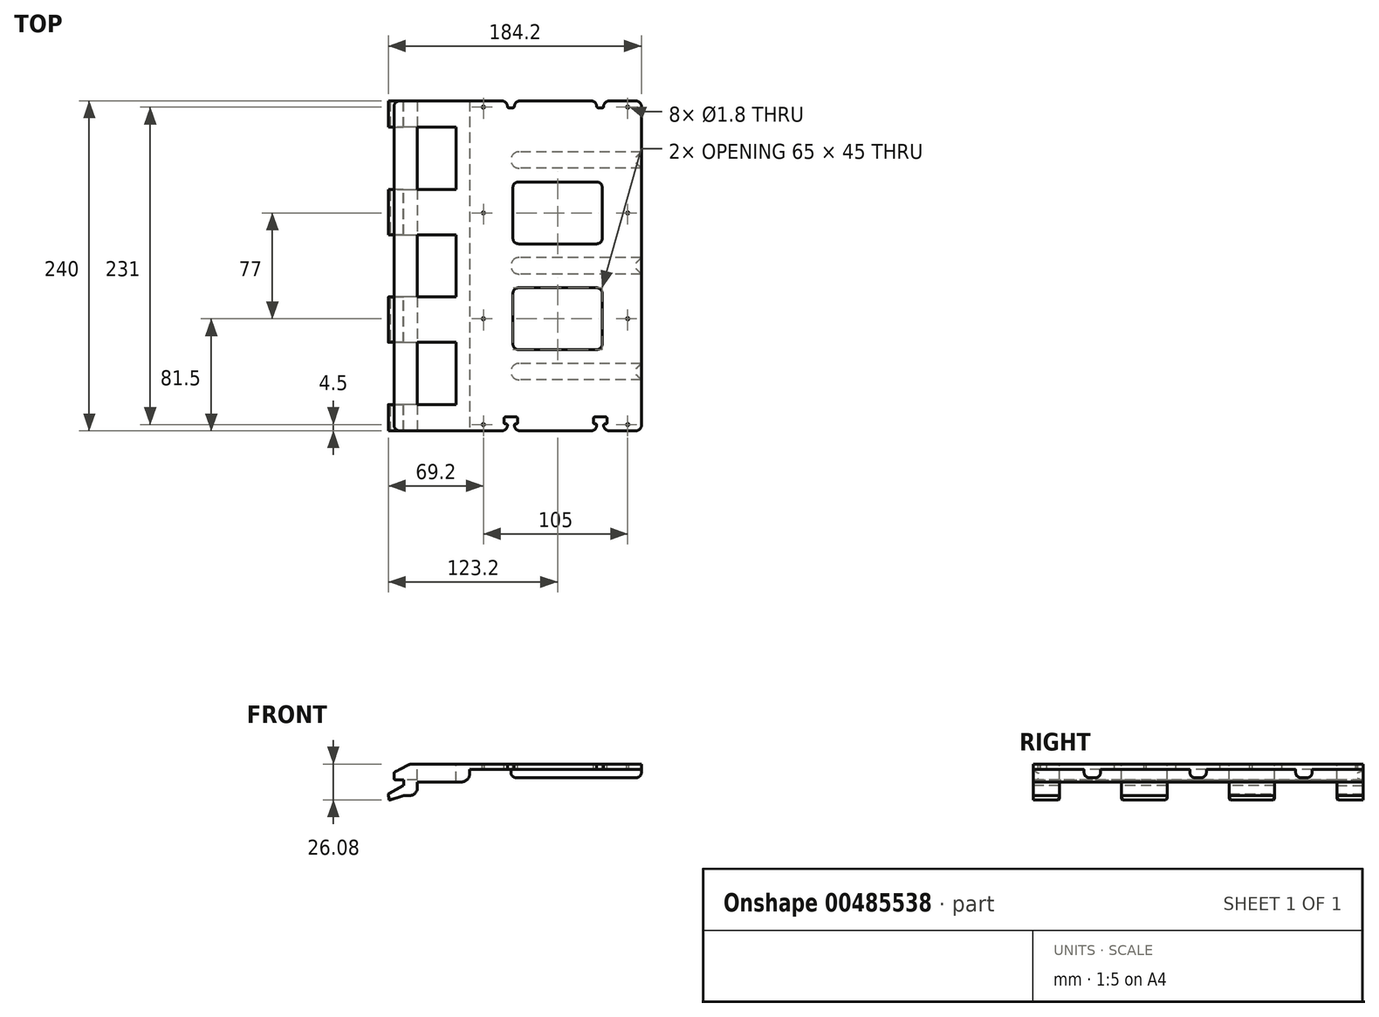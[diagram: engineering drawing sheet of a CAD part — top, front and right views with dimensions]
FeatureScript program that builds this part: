
annotation { "Feature Type Name" : "Feature", "Feature Type Description" : "" }
export const myFeature = defineFeature(function(context is Context, id is Id, definition is map)
    precondition{}
    {
        {
            var Q0;
            Q0=qCreatedBy(makeId("Top.planeOp"),FACE);
            var sketch = newSketch(context, id + "F0", { "sketchPlane" : qUnion([Q0])});
            skLineSegment(sketch, "E0", {"start": v(0, -197) * mm, "end": v(180, -197) * mm, "construction": true});
            skLineSegment(sketch, "E1", {"start": v(0, -43) * mm, "end": v(180, -43) * mm, "construction": true});
            skLineSegment(sketch, "E2", {"start": v(0, -158.5) * mm, "end": v(180, -158.5) * mm, "construction": true});
            skLineSegment(sketch, "E3", {"start": v(0, -81.5) * mm, "end": v(180, -81.5) * mm, "construction": true});
            skLineSegment(sketch, "E4", {"start": v(180, -203) * mm, "end": v(91, -203) * mm});
            skLineSegment(sketch, "E5", {"start": v(180, -191) * mm, "end": v(91, -191) * mm});
            skArc(sketch, "E6", {"start": v(91, -191) * mm, "mid": v(85, -197) * mm, "end": v(91, -203) * mm});
            skLineSegment(sketch, "E7", {"start": v(180, -126) * mm, "end": v(91, -126) * mm});
            skLineSegment(sketch, "E8", {"start": v(180, -114) * mm, "end": v(91, -114) * mm});
            skArc(sketch, "E9", {"start": v(91, -114) * mm, "mid": v(85, -120) * mm, "end": v(91, -126) * mm});
            skLineSegment(sketch, "E10", {"start": v(180, -49) * mm, "end": v(91, -49) * mm});
            skLineSegment(sketch, "E11", {"start": v(180, -37) * mm, "end": v(91, -37) * mm});
            skArc(sketch, "E12", {"start": v(91, -37) * mm, "mid": v(85, -43) * mm, "end": v(91, -49) * mm});
            skLineSegment(sketch, "E13", {"start": v(91, -240) * mm, "end": v(91, 0) * mm, "construction": true});
            skCircle(sketch, "E14", {"center": v(65, -158.5) * mm, "radius": 0.9 * mm});
            skCircle(sketch, "E15", {"center": v(65, -81.5) * mm, "radius": 0.9 * mm});
            skCircle(sketch, "E16", {"center": v(170, -158.5) * mm, "radius": 0.9 * mm});
            skCircle(sketch, "E17", {"center": v(170, -81.5) * mm, "radius": 0.9 * mm});
            skLineSegment(sketch, "E18.bottom", {"start": v(180, -240) * mm, "end": v(0, -240) * mm});
            skLineSegment(sketch, "E18.top", {"start": v(180, 0) * mm, "end": v(0, 0) * mm});
            skLineSegment(sketch, "E18.left", {"start": v(180, -240) * mm, "end": v(180, 0) * mm});
            skLineSegment(sketch, "E18.right", {"start": v(0, -240) * mm, "end": v(0, 0) * mm});
            skLineSegment(sketch, "E19", {"start": v(5, 0) * mm, "end": v(5, -240) * mm});
            skLineSegment(sketch, "E20", {"start": v(0, -120) * mm, "end": v(180, -120) * mm, "construction": true});
            skLineSegment(sketch, "E21", {"start": v(17, 0) * mm, "end": v(17, -240) * mm});
            skLineSegment(sketch, "E22", {"start": v(55, 0) * mm, "end": v(55, -240) * mm});
            skLineSegment(sketch, "E23", {"start": v(0, -97.4) * mm, "end": v(45, -97.4) * mm});
            skLineSegment(sketch, "E24", {"start": v(45, -97.4) * mm, "end": v(45, -142.6) * mm});
            skLineSegment(sketch, "E25", {"start": v(45, -142.6) * mm, "end": v(0, -142.6) * mm});
            skLineSegment(sketch, "E26", {"start": v(0, -175.7) * mm, "end": v(45, -175.7) * mm});
            skLineSegment(sketch, "E27", {"start": v(45, -175.7) * mm, "end": v(45, -220.9) * mm});
            skLineSegment(sketch, "E28", {"start": v(45, -220.9) * mm, "end": v(0, -220.9) * mm});
            skLineSegment(sketch, "E29", {"start": v(0, -64.3) * mm, "end": v(45, -64.3) * mm});
            skLineSegment(sketch, "E30", {"start": v(45, -64.3) * mm, "end": v(45, -19.1) * mm});
            skLineSegment(sketch, "E31", {"start": v(45, -19.1) * mm, "end": v(0, -19.1) * mm});
            skLineSegment(sketch, "E32", {"start": v(0, -235.5) * mm, "end": v(180, -235.5) * mm, "construction": true});
            skLineSegment(sketch, "E33", {"start": v(0, -4.5) * mm, "end": v(180, -4.5) * mm, "construction": true});
            skCircle(sketch, "E34", {"center": v(65, -235.5) * mm, "radius": 0.9 * mm});
            skCircle(sketch, "E35", {"center": v(65, -4.5) * mm, "radius": 0.9 * mm});
            skCircle(sketch, "E36", {"center": v(170, -4.5) * mm, "radius": 0.9 * mm});
            skCircle(sketch, "E37", {"center": v(170, -235.5) * mm, "radius": 0.9 * mm});
            skLineSegment(sketch, "E38.bottom", {"start": v(151.5, -104) * mm, "end": v(86.5, -104) * mm});
            skLineSegment(sketch, "E38.top", {"start": v(151.5, -59) * mm, "end": v(86.5, -59) * mm});
            skLineSegment(sketch, "E38.left", {"start": v(151.5, -104) * mm, "end": v(151.5, -59) * mm});
            skLineSegment(sketch, "E38.right", {"start": v(86.5, -104) * mm, "end": v(86.5, -59) * mm});
            skPoint(sketch, "E38.middle", {"position": v(119, -81.5) * mm});
            skLineSegment(sketch, "E39.bottom", {"start": v(151.5, -181) * mm, "end": v(86.5, -181) * mm});
            skLineSegment(sketch, "E39.top", {"start": v(151.5, -136) * mm, "end": v(86.5, -136) * mm});
            skLineSegment(sketch, "E39.left", {"start": v(151.5, -181) * mm, "end": v(151.5, -136) * mm});
            skLineSegment(sketch, "E39.right", {"start": v(86.5, -181) * mm, "end": v(86.5, -136) * mm});
            skPoint(sketch, "E39.middle", {"position": v(119, -158.5) * mm});
            skPoint(sketch, "E40.centerSnap0", {"position": v(119, -181) * mm});
            skLineSegment(sketch, "E41.bottom", {"start": v(82.5, -240) * mm, "end": v(87.5, -240) * mm});
            skLineSegment(sketch, "E41.top", {"start": v(82.5, -235) * mm, "end": v(87.5, -235) * mm});
            skLineSegment(sketch, "E41.left", {"start": v(82.5, -240) * mm, "end": v(82.5, -235) * mm});
            skLineSegment(sketch, "E41.right", {"start": v(87.5, -240) * mm, "end": v(87.5, -235) * mm});
            skLineSegment(sketch, "E42.bottom", {"start": v(80, -235) * mm, "end": v(90, -235) * mm});
            skLineSegment(sketch, "E42.top", {"start": v(80, -230) * mm, "end": v(90, -230) * mm});
            skLineSegment(sketch, "E42.left", {"start": v(80, -235) * mm, "end": v(80, -230) * mm});
            skLineSegment(sketch, "E42.right", {"start": v(90, -235) * mm, "end": v(90, -230) * mm});
            skLineSegment(sketch, "E43", {"start": v(85, -235) * mm, "end": v(85, -230) * mm, "construction": true});
            skLineSegment(sketch, "E44.bottom", {"start": v(147.5, -240) * mm, "end": v(152.5, -240) * mm});
            skLineSegment(sketch, "E44.top", {"start": v(147.5, -235) * mm, "end": v(152.5, -235) * mm});
            skLineSegment(sketch, "E44.left", {"start": v(147.5, -240) * mm, "end": v(147.5, -235) * mm});
            skLineSegment(sketch, "E44.right", {"start": v(152.5, -240) * mm, "end": v(152.5, -235) * mm});
            skLineSegment(sketch, "E45.bottom", {"start": v(145, -235) * mm, "end": v(155, -235) * mm});
            skLineSegment(sketch, "E45.top", {"start": v(145, -230) * mm, "end": v(155, -230) * mm});
            skLineSegment(sketch, "E45.left", {"start": v(145, -235) * mm, "end": v(145, -230) * mm});
            skLineSegment(sketch, "E45.right", {"start": v(155, -235) * mm, "end": v(155, -230) * mm});
            skLineSegment(sketch, "E46", {"start": v(150, -235) * mm, "end": v(150, -230) * mm, "construction": true});
            skLineSegment(sketch, "E47", {"start": v(150, -240) * mm, "end": v(150, -235) * mm, "construction": true});
            skLineSegment(sketch, "E48.bottom", {"start": v(152.5, 0) * mm, "end": v(147.5, 0) * mm});
            skLineSegment(sketch, "E48.top", {"start": v(152.5, -5) * mm, "end": v(147.5, -5) * mm});
            skLineSegment(sketch, "E48.left", {"start": v(152.5, 0) * mm, "end": v(152.5, -5) * mm});
            skLineSegment(sketch, "E48.right", {"start": v(147.5, 0) * mm, "end": v(147.5, -5) * mm});
            skLineSegment(sketch, "E49", {"start": v(150, 0) * mm, "end": v(150, -10) * mm, "construction": true});
            skPoint(sketch, "E49.endSnap0", {"position": v(150, -5) * mm});
            skLineSegment(sketch, "E50.bottom", {"start": v(145, -5) * mm, "end": v(155, -5) * mm});
            skLineSegment(sketch, "E50.top", {"start": v(145, -10) * mm, "end": v(155, -10) * mm});
            skLineSegment(sketch, "E50.left", {"start": v(145, -5) * mm, "end": v(145, -10) * mm});
            skLineSegment(sketch, "E50.right", {"start": v(155, -5) * mm, "end": v(155, -10) * mm});
            skLineSegment(sketch, "E51.bottom", {"start": v(82.5, 0) * mm, "end": v(87.5, 0) * mm});
            skLineSegment(sketch, "E51.top", {"start": v(82.5, -5) * mm, "end": v(87.5, -5) * mm});
            skLineSegment(sketch, "E51.left", {"start": v(82.5, 0) * mm, "end": v(82.5, -5) * mm});
            skLineSegment(sketch, "E51.right", {"start": v(87.5, 0) * mm, "end": v(87.5, -5) * mm});
            skLineSegment(sketch, "E52", {"start": v(85, 0) * mm, "end": v(85, -10) * mm, "construction": true});
            skLineSegment(sketch, "E53.bottom", {"start": v(90, -5) * mm, "end": v(80, -5) * mm});
            skLineSegment(sketch, "E53.top", {"start": v(90, -10) * mm, "end": v(80, -10) * mm});
            skLineSegment(sketch, "E53.left", {"start": v(90, -5) * mm, "end": v(90, -10) * mm});
            skLineSegment(sketch, "E53.right", {"start": v(80, -5) * mm, "end": v(80, -10) * mm});
            skSolve(sketch);
        }
        {
            var Q0;
            {var subQ7=sQuery(id+"F0.wireOp",EDGE,"E4");Q0=makeQuery(id+"F0.imprint","IMPRINT",FACE,{"disambiguationData":[TD([[makeQuery(id+"F0.imprint","IMPRINT",EDGE,{"derivedFrom":subQ7}),1.0]])]});}
            var Q1;
            {var subQ0=sQuery(id+"F0.wireOp",EDGE,"E4");Q1=makeQuery(id+"F0.imprint","IMPRINT",FACE,{"disambiguationData":[TD([[makeQuery(id+"F0.imprint","IMPRINT",EDGE,{"derivedFrom":subQ0}),-1.0]])]});}
            var Q2;
            {var subQ0=sQuery(id+"F0.wireOp",EDGE,"E7");Q2=makeQuery(id+"F0.imprint","IMPRINT",FACE,{"disambiguationData":[TD([[makeQuery(id+"F0.imprint","IMPRINT",EDGE,{"derivedFrom":subQ0}),-1.0]])]});}
            var Q3;
            {var subQ0=sQuery(id+"F0.wireOp",EDGE,"E10");Q3=makeQuery(id+"F0.imprint","IMPRINT",FACE,{"disambiguationData":[TD([[makeQuery(id+"F0.imprint","IMPRINT",EDGE,{"derivedFrom":subQ0}),-1.0]])]});}
            var Q4;
            Q4=makeQuery(id+"F0.imprint","IMPRINT",FACE,{"disambiguationData":[TD([[makeQuery(id+"F0.imprint","IMPRINT",EDGE,{"derivedFrom":sQuery(id+"F0.wireOp",EDGE,"E53.top")}),-1.0]])]});
            var Q5;
            Q5=makeQuery(id+"F0.imprint","IMPRINT",FACE,{"disambiguationData":[TD([[makeQuery(id+"F0.imprint","IMPRINT",EDGE,{"derivedFrom":sQuery(id+"F0.wireOp",EDGE,"E51.bottom")}),-1.0]])]});
            var Q6;
            Q6=makeQuery(id+"F0.imprint","IMPRINT",FACE,{"disambiguationData":[TD([[makeQuery(id+"F0.imprint","IMPRINT",EDGE,{"derivedFrom":sQuery(id+"F0.wireOp",EDGE,"E48.bottom")}),1.0]])]});
            var Q7;
            Q7=makeQuery(id+"F0.imprint","IMPRINT",FACE,{"disambiguationData":[TD([[makeQuery(id+"F0.imprint","IMPRINT",EDGE,{"derivedFrom":sQuery(id+"F0.wireOp",EDGE,"E50.top")}),1.0]])]});
            extrude(context, id + "F1", {"entities" : qUnion([Q0, Q1, Q2, Q3, Q4, Q5, Q6, Q7]), "oppositeDirection" : true, "depth" : 4 * mm});
        }
        {
            var Q0;
            {var subQ0=sQuery(id+"F0.wireOp",EDGE,"E21");Q0=makeQuery(id+"F0.imprint","IMPRINT",FACE,{"disambiguationData":[TD([[makeQuery(id+"F0.imprint","IMPRINT",EDGE,{"derivedFrom":subQ0}),1.0]])]});}
            var Q1;
            {var subQ5=sQuery(id+"F0.wireOp",EDGE,"n4lQ4PQO-9XsQ-tz0W-XekK-HpTfJCge4sbG");Q1=makeQuery(id+"F0.imprint","IMPRINT",FACE,{"disambiguationData":[TD([[makeQuery(id+"F0.imprint","IMPRINT",EDGE,{"derivedFrom":subQ5}),1.0]])]});}
            var Q2;
            {var subQ5=sQuery(id+"F0.wireOp",EDGE,"NRY2d1nv-D3un-2PJu-Z2eF-jLOu5DY2E8th");Q2=makeQuery(id+"F0.imprint","IMPRINT",FACE,{"disambiguationData":[TD([[makeQuery(id+"F0.imprint","IMPRINT",EDGE,{"derivedFrom":subQ5}),1.0]])]});}
            extrude(context, id + "F2", {"entities" : qUnion([Q0, Q1, Q2]), "operationType" : NewBodyOperationType.ADD, "oppositeDirection" : true, "depth" : 13 * mm});
        }
        {
            var Q0;
            {var subQ0=sQuery(id+"F0.wireOp",EDGE,"E19");var subQ1=sQuery(id+"F0.wireOp",EDGE,"E18.bottom");var subQ2=makeQuery(id+"F0.imprint","INTERSECT",VERTEX,{"derivedFrom":[subQ1,subQ0]});Q0=makeQuery(id+"F0.imprint","IMPRINT",FACE,{"disambiguationData":[TD([[makeQuery(id+"F0.imprint","IMPRINT",EDGE,{"disambiguationData":[TD([[subQ2,1.0]])],"derivedFrom":subQ1}),-1.0]])]});}
            var Q1;
            {var subQ0=sQuery(id+"F0.wireOp",EDGE,"E19");var subQ1=sQuery(id+"F0.wireOp",EDGE,"E18.top");var subQ2=makeQuery(id+"F0.imprint","INTERSECT",VERTEX,{"derivedFrom":[subQ1,subQ0]});Q1=makeQuery(id+"F0.imprint","IMPRINT",FACE,{"disambiguationData":[TD([[makeQuery(id+"F0.imprint","IMPRINT",EDGE,{"disambiguationData":[TD([[subQ2,1.0]])],"derivedFrom":subQ1}),1.0]])]});}
            var Q2;
            {var subQ0=sQuery(id+"F0.wireOp",EDGE,"E29");var subQ1=sQuery(id+"F0.wireOp",EDGE,"E19");var subQ2=makeQuery(id+"F0.imprint","INTERSECT",VERTEX,{"derivedFrom":[subQ1,subQ0]});Q2=makeQuery(id+"F0.imprint","IMPRINT",FACE,{"disambiguationData":[TD([[makeQuery(id+"F0.imprint","IMPRINT",EDGE,{"disambiguationData":[TD([[subQ2,-1.0]])],"derivedFrom":subQ1}),1.0]])]});}
            var Q3;
            {var subQ0=sQuery(id+"F0.wireOp",EDGE,"E25");var subQ1=sQuery(id+"F0.wireOp",EDGE,"E19");var subQ2=makeQuery(id+"F0.imprint","INTERSECT",VERTEX,{"derivedFrom":[subQ1,subQ0]});Q3=makeQuery(id+"F0.imprint","IMPRINT",FACE,{"disambiguationData":[TD([[makeQuery(id+"F0.imprint","IMPRINT",EDGE,{"disambiguationData":[TD([[subQ2,-1.0]])],"derivedFrom":subQ1}),1.0]])]});}
            extrude(context, id + "F3", {"entities" : qUnion([Q0, Q1, Q2, Q3]), "operationType" : NewBodyOperationType.ADD, "oppositeDirection" : true, "depth" : 23 * mm});
        }
        {
            var Q0;
            {var subQ0=sQuery(id+"F0.wireOp",EDGE,"E18.right");var subQ1=sQuery(id+"F0.wireOp",EDGE,"E18.bottom");var subQ2=makeQuery(id+"F0.imprint","INTERSECT",VERTEX,{"derivedFrom":[subQ1,subQ0]});Q0=makeQuery(id+"F0.imprint","IMPRINT",FACE,{"disambiguationData":[TD([[makeQuery(id+"F0.imprint","IMPRINT",EDGE,{"disambiguationData":[TD([[subQ2,1.0]])],"derivedFrom":subQ1}),-1.0]])]});}
            var Q1;
            {var subQ0=sQuery(id+"F0.wireOp",EDGE,"E18.right");var subQ1=sQuery(id+"F0.wireOp",EDGE,"E18.top");var subQ2=makeQuery(id+"F0.imprint","INTERSECT",VERTEX,{"derivedFrom":[subQ1,subQ0]});Q1=makeQuery(id+"F0.imprint","IMPRINT",FACE,{"disambiguationData":[TD([[makeQuery(id+"F0.imprint","IMPRINT",EDGE,{"disambiguationData":[TD([[subQ2,1.0]])],"derivedFrom":subQ1}),1.0]])]});}
            var Q2;
            {var subQ0=sQuery(id+"F0.wireOp",EDGE,"E25");var subQ1=sQuery(id+"F0.wireOp",EDGE,"E18.right");var subQ2=makeQuery(id+"F0.imprint","INTERSECT",VERTEX,{"derivedFrom":[subQ1,subQ0]});Q2=makeQuery(id+"F0.imprint","IMPRINT",FACE,{"disambiguationData":[TD([[makeQuery(id+"F0.imprint","IMPRINT",EDGE,{"disambiguationData":[TD([[subQ2,1.0]])],"derivedFrom":subQ1}),-1.0]])]});}
            var Q3;
            {var subQ0=sQuery(id+"F0.wireOp",EDGE,"E23");var subQ1=sQuery(id+"F0.wireOp",EDGE,"E18.right");var subQ2=makeQuery(id+"F0.imprint","INTERSECT",VERTEX,{"derivedFrom":[subQ1,subQ0]});Q3=makeQuery(id+"F0.imprint","IMPRINT",FACE,{"disambiguationData":[TD([[makeQuery(id+"F0.imprint","IMPRINT",EDGE,{"disambiguationData":[TD([[subQ2,-1.0]])],"derivedFrom":subQ1}),-1.0]])]});}
            var Q4;
            {var subQ0=sQuery(id+"F0.wireOp",EDGE,"E26");var subQ1=sQuery(id+"F0.wireOp",EDGE,"E18.right");var subQ2=makeQuery(id+"F0.imprint","INTERSECT",VERTEX,{"derivedFrom":[subQ1,subQ0]});Q4=makeQuery(id+"F0.imprint","IMPRINT",FACE,{"disambiguationData":[TD([[makeQuery(id+"F0.imprint","IMPRINT",EDGE,{"disambiguationData":[TD([[subQ2,1.0]])],"derivedFrom":subQ1}),-1.0]])]});}
            var Q5;
            {var subQ0=sQuery(id+"F0.wireOp",EDGE,"E23");var subQ1=sQuery(id+"F0.wireOp",EDGE,"E18.right");var subQ2=makeQuery(id+"F0.imprint","INTERSECT",VERTEX,{"derivedFrom":[subQ1,subQ0]});Q5=makeQuery(id+"F0.imprint","IMPRINT",FACE,{"disambiguationData":[TD([[makeQuery(id+"F0.imprint","IMPRINT",EDGE,{"disambiguationData":[TD([[subQ2,1.0]])],"derivedFrom":subQ1}),-1.0]])]});}
            var Q6;
            {var subQ0=sQuery(id+"F0.wireOp",EDGE,"E29");var subQ1=sQuery(id+"F0.wireOp",EDGE,"E18.right");var subQ2=makeQuery(id+"F0.imprint","INTERSECT",VERTEX,{"derivedFrom":[subQ1,subQ0]});Q6=makeQuery(id+"F0.imprint","IMPRINT",FACE,{"disambiguationData":[TD([[makeQuery(id+"F0.imprint","IMPRINT",EDGE,{"disambiguationData":[TD([[subQ2,-1.0]])],"derivedFrom":subQ1}),-1.0]])]});}
            var Q7;
            {var subQ0=sQuery(id+"F0.wireOp",EDGE,"E26");var subQ1=sQuery(id+"F0.wireOp",EDGE,"E19");var subQ2=makeQuery(id+"F0.imprint","INTERSECT",VERTEX,{"derivedFrom":[subQ1,subQ0]});Q7=makeQuery(id+"F0.imprint","IMPRINT",FACE,{"disambiguationData":[TD([[makeQuery(id+"F0.imprint","IMPRINT",EDGE,{"disambiguationData":[TD([[subQ2,-1.0]])],"derivedFrom":subQ1}),1.0]])]});}
            var Q8;
            {var subQ0=sQuery(id+"F0.wireOp",EDGE,"E23");var subQ1=sQuery(id+"F0.wireOp",EDGE,"E19");var subQ2=makeQuery(id+"F0.imprint","INTERSECT",VERTEX,{"derivedFrom":[subQ1,subQ0]});Q8=makeQuery(id+"F0.imprint","IMPRINT",FACE,{"disambiguationData":[TD([[makeQuery(id+"F0.imprint","IMPRINT",EDGE,{"disambiguationData":[TD([[subQ2,-1.0]])],"derivedFrom":subQ1}),1.0]])]});}
            var Q9;
            {var subQ0=sQuery(id+"F0.wireOp",EDGE,"E31");var subQ1=sQuery(id+"F0.wireOp",EDGE,"E19");var subQ2=makeQuery(id+"F0.imprint","INTERSECT",VERTEX,{"derivedFrom":[subQ1,subQ0]});Q9=makeQuery(id+"F0.imprint","IMPRINT",FACE,{"disambiguationData":[TD([[makeQuery(id+"F0.imprint","IMPRINT",EDGE,{"disambiguationData":[TD([[subQ2,-1.0]])],"derivedFrom":subQ1}),1.0]])]});}
            var Q10;
            Q10=makeQuery(id+"F2.opExtrude","CAP_FACE",FACE,{"disambiguationData":[OSD([sQuery(id+"F0.wireOp",EDGE,"E14"),sQuery(id+"F0.wireOp",EDGE,"E15"),sQuery(id+"F0.wireOp",EDGE,"E18.bottom"),sQuery(id+"F0.wireOp",EDGE,"E18.top"),sQuery(id+"F0.wireOp",EDGE,"E21"),sQuery(id+"F0.wireOp",EDGE,"E22")])],"isStart":false});
            extrude(context, id + "F4", {"entities" : qUnion([Q0, Q1, Q2, Q3, Q4, Q5, Q6, Q7, Q8, Q9]), "operationType" : NewBodyOperationType.ADD, "oppositeDirection" : true, "endBoundEntityFace" : qUnion([Q10]), "depth" : 11.5 * mm});
        }
        {
            var Q0;
            {var subQ0=sQuery(id+"F0.wireOp",EDGE,"E18.bottom");Q0=makeQuery(id+"F4.boolean.opBoolean","MERGE",FACE,{"derivedFrom":[makeQuery(id+"F3.boolean.opBoolean","MERGE",FACE,{"derivedFrom":[makeQuery(id+"F2.boolean.opBoolean","MERGE",FACE,{"derivedFrom":[makeQuery(id+"F1.opExtrude","SWEPT_FACE",FACE,{"disambiguationData":[OSD([subQ0])]}),makeQuery(id+"F2.opExtrude","SWEPT_FACE",FACE,{"disambiguationData":[OSD([subQ0])]})]}),makeQuery(id+"F3.opExtrude","SWEPT_FACE",FACE,{"disambiguationData":[OSD([subQ0])]})]}),makeQuery(id+"F4.opExtrude","SWEPT_FACE",FACE,{"disambiguationData":[OSD([subQ0])]})]});}
            var sketch = newSketch(context, id + "F5", { "sketchPlane" : qUnion([Q0])});
            skLineSegment(sketch, "E54.bottom", {"start": v(5, -11.5) * mm, "end": v(7, -11.5) * mm});
            skLineSegment(sketch, "E54.top", {"start": v(5, -15.5) * mm, "end": v(7, -15.5) * mm});
            skLineSegment(sketch, "E54.left", {"start": v(5, -11.5) * mm, "end": v(5, -15.5) * mm});
            skLineSegment(sketch, "E54.right", {"start": v(7, -11.5) * mm, "end": v(7, -15.5) * mm});
            skSolve(sketch);
        }
        {
            var Q0;
            Q0=makeQuery(id+"F5.imprint","IMPRINT",FACE,{"disambiguationData":[TD([[makeQuery(id+"F5.imprint","IMPRINT",EDGE,{"derivedFrom":sQuery(id+"F5.wireOp",EDGE,"E54.bottom")}),-1.0]])]});
            var Q1;
            {var subQ0=sQuery(id+"F0.wireOp",EDGE,"E18.top");Q1=makeQuery(id+"F4.boolean.opBoolean","MERGE",FACE,{"derivedFrom":[makeQuery(id+"F3.boolean.opBoolean","MERGE",FACE,{"derivedFrom":[makeQuery(id+"F2.boolean.opBoolean","MERGE",FACE,{"derivedFrom":[makeQuery(id+"F1.opExtrude","SWEPT_FACE",FACE,{"disambiguationData":[OSD([subQ0])]}),makeQuery(id+"F2.opExtrude","SWEPT_FACE",FACE,{"disambiguationData":[OSD([subQ0])]})]}),makeQuery(id+"F3.opExtrude","SWEPT_FACE",FACE,{"disambiguationData":[OSD([subQ0])]})]}),makeQuery(id+"F4.opExtrude","SWEPT_FACE",FACE,{"disambiguationData":[OSD([subQ0])]})]});}
            extrude(context, id + "F6", {"entities" : qUnion([Q0]), "operationType" : NewBodyOperationType.REMOVE, "oppositeDirection" : true, "endBoundEntityFace" : qUnion([Q1]), "depth" : 300 * mm});
        }
        {
            var Q0;
            {var subQ0=sQuery(id+"F0.wireOp",EDGE,"E4");Q0=makeQuery(id+"F0.imprint","IMPRINT",FACE,{"disambiguationData":[TD([[makeQuery(id+"F0.imprint","IMPRINT",EDGE,{"derivedFrom":subQ0}),-1.0]])]});}
            var Q1;
            {var subQ0=sQuery(id+"F0.wireOp",EDGE,"E7");Q1=makeQuery(id+"F0.imprint","IMPRINT",FACE,{"disambiguationData":[TD([[makeQuery(id+"F0.imprint","IMPRINT",EDGE,{"derivedFrom":subQ0}),-1.0]])]});}
            var Q2;
            {var subQ0=sQuery(id+"F0.wireOp",EDGE,"E10");Q2=makeQuery(id+"F0.imprint","IMPRINT",FACE,{"disambiguationData":[TD([[makeQuery(id+"F0.imprint","IMPRINT",EDGE,{"derivedFrom":subQ0}),-1.0]])]});}
            extrude(context, id + "F7", {"entities" : qUnion([Q0, Q1, Q2]), "operationType" : NewBodyOperationType.ADD, "oppositeDirection" : true, "depth" : 10 * mm});
        }
        {
            var Q0;
            Q0=makeQuery(id+"F7.opExtrude","CAP_FACE",FACE,{"disambiguationData":[OSD([sQuery(id+"F0.wireOp",EDGE,"E10"),sQuery(id+"F0.wireOp",EDGE,"E11"),sQuery(id+"F0.wireOp",EDGE,"E12"),sQuery(id+"F0.wireOp",EDGE,"E18.left")])],"isStart":false});
            var Q1;
            Q1=makeQuery(id+"F7.opExtrude","CAP_FACE",FACE,{"disambiguationData":[OSD([sQuery(id+"F0.wireOp",EDGE,"E7"),sQuery(id+"F0.wireOp",EDGE,"E8"),sQuery(id+"F0.wireOp",EDGE,"E9"),sQuery(id+"F0.wireOp",EDGE,"E18.left")])],"isStart":false});
            var Q2;
            Q2=makeQuery(id+"F7.opExtrude","CAP_FACE",FACE,{"disambiguationData":[OSD([sQuery(id+"F0.wireOp",EDGE,"E4"),sQuery(id+"F0.wireOp",EDGE,"E5"),sQuery(id+"F0.wireOp",EDGE,"E6"),sQuery(id+"F0.wireOp",EDGE,"E18.left")])],"isStart":false});
            var Q3;
            Q3=makeQuery(id+"F1.opExtrude","SWEPT_EDGE",EDGE,{"disambiguationData":[OSD([sQuery(id+"F0.wireOp",EDGE,"E38.top"),sQuery(id+"F0.wireOp",EDGE,"E38.right")])]});
            var Q4;
            Q4=makeQuery(id+"F1.opExtrude","SWEPT_EDGE",EDGE,{"disambiguationData":[OSD([sQuery(id+"F0.wireOp",EDGE,"E38.bottom"),sQuery(id+"F0.wireOp",EDGE,"E38.right")])]});
            var Q5;
            Q5=makeQuery(id+"F1.opExtrude","SWEPT_EDGE",EDGE,{"disambiguationData":[OSD([sQuery(id+"F0.wireOp",EDGE,"E38.top"),sQuery(id+"F0.wireOp",EDGE,"E38.left")])]});
            var Q6;
            Q6=makeQuery(id+"F1.opExtrude","SWEPT_EDGE",EDGE,{"disambiguationData":[OSD([sQuery(id+"F0.wireOp",EDGE,"E38.bottom"),sQuery(id+"F0.wireOp",EDGE,"E38.left")])]});
            var Q7;
            Q7=makeQuery(id+"F1.opExtrude","SWEPT_EDGE",EDGE,{"disambiguationData":[OSD([sQuery(id+"F0.wireOp",EDGE,"E39.top"),sQuery(id+"F0.wireOp",EDGE,"E39.left")])]});
            var Q8;
            {var subQ0=sQuery(id+"F0.wireOp",EDGE,"E40");var subQ1=sQuery(id+"F0.wireOp",EDGE,"E18.bottom");Q8=makeQuery(id+"F1.opExtrude","SWEPT_EDGE",EDGE,{"disambiguationData":[OSD([subQ1,subQ0]),TDD([makeQuery(id+"F0.imprint","INTERSECT",VERTEX,{"disambiguationData":[OD(1.0)],"derivedFrom":[subQ1,subQ0]})])]});}
            var Q9;
            Q9=makeQuery(id+"F1.opExtrude","SWEPT_EDGE",EDGE,{"disambiguationData":[OSD([sQuery(id+"F0.wireOp",EDGE,"E39.bottom"),sQuery(id+"F0.wireOp",EDGE,"E39.right")])]});
            var Q10;
            Q10=makeQuery(id+"F1.opExtrude","SWEPT_EDGE",EDGE,{"disambiguationData":[OSD([sQuery(id+"F0.wireOp",EDGE,"E39.top"),sQuery(id+"F0.wireOp",EDGE,"E39.right")])]});
            var Q11;
            {var subQ0=sQuery(id+"F0.wireOp",EDGE,"dDL4M1PI-aelY-u7zt-lnq0-sMzwrNtlq2yo");var subQ1=sQuery(id+"F0.wireOp",EDGE,"E18.top");Q11=makeQuery(id+"F1.opExtrude","SWEPT_EDGE",EDGE,{"disambiguationData":[OSD([subQ1,subQ0]),TDD([makeQuery(id+"F0.imprint","INTERSECT",VERTEX,{"disambiguationData":[OD(1.0)],"derivedFrom":[subQ1,subQ0]})])]});}
            var Q12;
            {var subQ0=sQuery(id+"F0.wireOp",EDGE,"dDL4M1PI-aelY-u7zt-lnq0-sMzwrNtlq2yo");var subQ1=sQuery(id+"F0.wireOp",EDGE,"E18.top");Q12=makeQuery(id+"F1.opExtrude","SWEPT_EDGE",EDGE,{"disambiguationData":[OSD([subQ1,subQ0]),TDD([makeQuery(id+"F0.imprint","INTERSECT",VERTEX,{"disambiguationData":[OD(0.0)],"derivedFrom":[subQ1,subQ0]})])]});}
            var Q13;
            Q13=makeQuery(id+"F1.opExtrude","SWEPT_EDGE",EDGE,{"disambiguationData":[OSD([sQuery(id+"F0.wireOp",EDGE,"E39.bottom"),sQuery(id+"F0.wireOp",EDGE,"E39.left")])]});
            var Q14;
            {var subQ0=sQuery(id+"F0.wireOp",EDGE,"E40");var subQ1=sQuery(id+"F0.wireOp",EDGE,"E18.bottom");Q14=makeQuery(id+"F1.opExtrude","SWEPT_EDGE",EDGE,{"disambiguationData":[OSD([subQ1,subQ0]),TDD([makeQuery(id+"F0.imprint","INTERSECT",VERTEX,{"disambiguationData":[OD(0.0)],"derivedFrom":[subQ1,subQ0]})])]});}
            var Q15;
            Q15=makeQuery(id+"F1.opExtrude","SWEPT_EDGE",EDGE,{"disambiguationData":[OSD([sQuery(id+"F0.wireOp",EDGE,"E18.bottom"),sQuery(id+"F0.wireOp",EDGE,"E18.left")])]});
            var Q16;
            Q16=makeQuery(id+"F1.opExtrude","SWEPT_EDGE",EDGE,{"disambiguationData":[OSD([sQuery(id+"F0.wireOp",EDGE,"E18.top"),sQuery(id+"F0.wireOp",EDGE,"E18.left")])]});
            var Q17;
            Q17=makeQuery(id+"F4.opExtrude","SWEPT_EDGE",EDGE,{"disambiguationData":[OSD([sQuery(id+"F0.wireOp",EDGE,"E18.top"),sQuery(id+"F0.wireOp",EDGE,"E18.right")])]});
            var Q18;
            Q18=makeQuery(id+"F4.opExtrude","SWEPT_EDGE",EDGE,{"disambiguationData":[OSD([sQuery(id+"F0.wireOp",EDGE,"E18.bottom"),sQuery(id+"F0.wireOp",EDGE,"E18.right")])]});
            fillet(context, id + "F8", {"entities" : qUnion([Q0, Q1, Q2, Q3, Q4, Q5, Q6, Q7, Q8, Q9, Q10, Q11, Q12, Q13, Q14, Q15, Q16, Q17, Q18]), "radius" : 4 * mm, "tangentPropagation" : true, "allowEdgeOverflow" : false});
        }
        {
            var Q0;
            Q0=makeQuery(id+"F4.opExtrude","CAP_EDGE",EDGE,{"disambiguationData":[OSD([sQuery(id+"F0.wireOp",EDGE,"E18.right")])],"isStart":true});
            chamfer(context, id + "F9", {"entities" : qUnion([Q0]), "chamferType" : ChamferType.TWO_OFFSETS, "width1" : 6 * mm, "oppositeDirection" : false, "width2" : 12 * mm});
        }
        {
            var Q0;
            {var subQ0=sQuery(id+"F0.wireOp",EDGE,"E19");Q0=makeQuery(id+"F3.opExtrude","CAP_EDGE",EDGE,{"disambiguationData":[OSD([subQ0]),TDD([makeQuery(id+"F0.imprint","IMPRINT",EDGE,{"disambiguationData":[TD([[makeQuery(id+"F0.imprint","INTERSECT",VERTEX,{"derivedFrom":[sQuery(id+"F0.wireOp",EDGE,"E18.bottom"),subQ0]}),1.0]])],"derivedFrom":subQ0})])],"isStart":false});}
            var Q1;
            {var subQ0=sQuery(id+"F0.wireOp",EDGE,"E19");Q1=makeQuery(id+"F3.opExtrude","CAP_EDGE",EDGE,{"disambiguationData":[OSD([subQ0]),TDD([makeQuery(id+"F0.imprint","IMPRINT",EDGE,{"disambiguationData":[TD([[makeQuery(id+"F0.imprint","INTERSECT",VERTEX,{"derivedFrom":[subQ0,sQuery(id+"F0.wireOp",EDGE,"E25")]}),-1.0]])],"derivedFrom":subQ0})])],"isStart":false});}
            var Q2;
            {var subQ0=sQuery(id+"F0.wireOp",EDGE,"E19");Q2=makeQuery(id+"F3.opExtrude","CAP_EDGE",EDGE,{"disambiguationData":[OSD([subQ0]),TDD([makeQuery(id+"F0.imprint","IMPRINT",EDGE,{"disambiguationData":[TD([[makeQuery(id+"F0.imprint","INTERSECT",VERTEX,{"derivedFrom":[subQ0,sQuery(id+"F0.wireOp",EDGE,"E29")]}),-1.0]])],"derivedFrom":subQ0})])],"isStart":false});}
            var Q3;
            {var subQ0=sQuery(id+"F0.wireOp",EDGE,"E19");Q3=makeQuery(id+"F3.opExtrude","CAP_EDGE",EDGE,{"disambiguationData":[OSD([subQ0]),TDD([makeQuery(id+"F0.imprint","IMPRINT",EDGE,{"disambiguationData":[TD([[makeQuery(id+"F0.imprint","INTERSECT",VERTEX,{"derivedFrom":[sQuery(id+"F0.wireOp",EDGE,"E18.top"),subQ0]}),-1.0]])],"derivedFrom":subQ0})])],"isStart":false});}
            chamfer(context, id + "F10", {"entities" : qUnion([Q0, Q1, Q2, Q3]), "chamferType" : ChamferType.TWO_OFFSETS, "width1" : 20 * mm, "oppositeDirection" : false, "width2" : 2 * mm});
        }
        {
            var Q0;
            {var subQ0=sQuery(id+"F0.wireOp",EDGE,"E19");Q0=makeQuery(id+"F10.opChamfer","BLEND_FACE",FACE,{"disambiguationData":[OSD([subQ0]),TDD([makeQuery(id+"F3.opExtrude","CAP_EDGE",EDGE,{"disambiguationData":[OSD([subQ0]),TDD([makeQuery(id+"F0.imprint","IMPRINT",EDGE,{"disambiguationData":[TD([[makeQuery(id+"F0.imprint","INTERSECT",VERTEX,{"derivedFrom":[sQuery(id+"F0.wireOp",EDGE,"E18.bottom"),subQ0]}),1.0]])],"derivedFrom":subQ0})])],"isStart":false})])]});}
            var Q1;
            {var subQ0=sQuery(id+"F0.wireOp",EDGE,"E19");Q1=makeQuery(id+"F10.opChamfer","BLEND_FACE",FACE,{"disambiguationData":[OSD([subQ0]),TDD([makeQuery(id+"F3.opExtrude","CAP_EDGE",EDGE,{"disambiguationData":[OSD([subQ0]),TDD([makeQuery(id+"F0.imprint","IMPRINT",EDGE,{"disambiguationData":[TD([[makeQuery(id+"F0.imprint","INTERSECT",VERTEX,{"derivedFrom":[subQ0,sQuery(id+"F0.wireOp",EDGE,"E25")]}),-1.0]])],"derivedFrom":subQ0})])],"isStart":false})])]});}
            var Q2;
            {var subQ0=sQuery(id+"F0.wireOp",EDGE,"E19");Q2=makeQuery(id+"F10.opChamfer","BLEND_FACE",FACE,{"disambiguationData":[OSD([subQ0]),TDD([makeQuery(id+"F3.opExtrude","CAP_EDGE",EDGE,{"disambiguationData":[OSD([subQ0]),TDD([makeQuery(id+"F0.imprint","IMPRINT",EDGE,{"disambiguationData":[TD([[makeQuery(id+"F0.imprint","INTERSECT",VERTEX,{"derivedFrom":[subQ0,sQuery(id+"F0.wireOp",EDGE,"E29")]}),-1.0]])],"derivedFrom":subQ0})])],"isStart":false})])]});}
            var Q3;
            {var subQ0=sQuery(id+"F0.wireOp",EDGE,"E19");Q3=makeQuery(id+"F10.opChamfer","BLEND_FACE",FACE,{"disambiguationData":[OSD([subQ0]),TDD([makeQuery(id+"F3.opExtrude","CAP_EDGE",EDGE,{"disambiguationData":[OSD([subQ0]),TDD([makeQuery(id+"F0.imprint","IMPRINT",EDGE,{"disambiguationData":[TD([[makeQuery(id+"F0.imprint","INTERSECT",VERTEX,{"derivedFrom":[sQuery(id+"F0.wireOp",EDGE,"E18.top"),subQ0]}),-1.0]])],"derivedFrom":subQ0})])],"isStart":false})])]});}
            extrude(context, id + "F11", {"entities" : qUnion([Q0, Q1, Q2, Q3]), "operationType" : NewBodyOperationType.ADD, "depth" : 7 * mm});
        }
        {
            var Q0;
            {var subQ0=sQuery(id+"F0.wireOp",EDGE,"E19");Q0=makeQuery(id+"F11.opExtrude","CAP_FACE",FACE,{"disambiguationData":[OSD([subQ0]),TDD([makeQuery(id+"F10.opChamfer","BLEND_FACE",FACE,{"disambiguationData":[OSD([subQ0]),TDD([makeQuery(id+"F3.opExtrude","CAP_EDGE",EDGE,{"disambiguationData":[OSD([subQ0]),TDD([makeQuery(id+"F0.imprint","IMPRINT",EDGE,{"disambiguationData":[TD([[makeQuery(id+"F0.imprint","INTERSECT",VERTEX,{"derivedFrom":[sQuery(id+"F0.wireOp",EDGE,"E18.bottom"),subQ0]}),1.0]])],"derivedFrom":subQ0})])],"isStart":false})])]})])],"isStart":false});}
            var Q1;
            {var subQ0=sQuery(id+"F0.wireOp",EDGE,"E19");Q1=makeQuery(id+"F11.opExtrude","CAP_FACE",FACE,{"disambiguationData":[OSD([subQ0]),TDD([makeQuery(id+"F10.opChamfer","BLEND_FACE",FACE,{"disambiguationData":[OSD([subQ0]),TDD([makeQuery(id+"F3.opExtrude","CAP_EDGE",EDGE,{"disambiguationData":[OSD([subQ0]),TDD([makeQuery(id+"F0.imprint","IMPRINT",EDGE,{"disambiguationData":[TD([[makeQuery(id+"F0.imprint","INTERSECT",VERTEX,{"derivedFrom":[subQ0,sQuery(id+"F0.wireOp",EDGE,"E25")]}),-1.0]])],"derivedFrom":subQ0})])],"isStart":false})])]})])],"isStart":false});}
            var Q2;
            {var subQ0=sQuery(id+"F0.wireOp",EDGE,"E19");Q2=makeQuery(id+"F11.opExtrude","CAP_FACE",FACE,{"disambiguationData":[OSD([subQ0]),TDD([makeQuery(id+"F10.opChamfer","BLEND_FACE",FACE,{"disambiguationData":[OSD([subQ0]),TDD([makeQuery(id+"F3.opExtrude","CAP_EDGE",EDGE,{"disambiguationData":[OSD([subQ0]),TDD([makeQuery(id+"F0.imprint","IMPRINT",EDGE,{"disambiguationData":[TD([[makeQuery(id+"F0.imprint","INTERSECT",VERTEX,{"derivedFrom":[subQ0,sQuery(id+"F0.wireOp",EDGE,"E29")]}),-1.0]])],"derivedFrom":subQ0})])],"isStart":false})])]})])],"isStart":false});}
            var Q3;
            {var subQ0=sQuery(id+"F0.wireOp",EDGE,"E19");Q3=makeQuery(id+"F11.opExtrude","CAP_FACE",FACE,{"disambiguationData":[OSD([subQ0]),TDD([makeQuery(id+"F10.opChamfer","BLEND_FACE",FACE,{"disambiguationData":[OSD([subQ0]),TDD([makeQuery(id+"F3.opExtrude","CAP_EDGE",EDGE,{"disambiguationData":[OSD([subQ0]),TDD([makeQuery(id+"F0.imprint","IMPRINT",EDGE,{"disambiguationData":[TD([[makeQuery(id+"F0.imprint","INTERSECT",VERTEX,{"derivedFrom":[sQuery(id+"F0.wireOp",EDGE,"E18.top"),subQ0]}),-1.0]])],"derivedFrom":subQ0})])],"isStart":false})])]})])],"isStart":false});}
            extrude(context, id + "F12", {"entities" : qUnion([Q0, Q1, Q2, Q3]), "operationType" : NewBodyOperationType.ADD, "depth" : 4 * mm});
        }
        {
            var Q0;
            Q0=makeQuery(id+"F12.opExtrude","CAP_EDGE",EDGE,{"disambiguationData":[OSD([sQuery(id+"F0.wireOp",EDGE,"E19"),sQuery(id+"F5.wireOp",EDGE,"E54.top")])],"isStart":false});
            chamfer(context, id + "F13", {"entities" : qUnion([Q0]), "chamferType" : ChamferType.TWO_OFFSETS, "width1" : 11.5 * mm, "oppositeDirection" : false, "width2" : 5 * mm, "tangentPropagation" : true});
        }
        {
            var Q0;
            {var subQ0=sQuery(id+"F0.wireOp",EDGE,"E21");Q0=makeQuery(id+"F3.opExtrude","CAP_EDGE",EDGE,{"disambiguationData":[OSD([subQ0]),TDD([makeQuery(id+"F0.imprint","IMPRINT",EDGE,{"disambiguationData":[TD([[makeQuery(id+"F0.imprint","INTERSECT",VERTEX,{"derivedFrom":[subQ0,sQuery(id+"F0.wireOp",EDGE,"E25")]}),-1.0]])],"derivedFrom":subQ0})])],"isStart":false});}
            var Q1;
            Q1=makeQuery(id+"F2.opExtrude","CAP_EDGE",EDGE,{"disambiguationData":[OSD([sQuery(id+"F0.wireOp",EDGE,"E22")])],"isStart":false});
            var Q2;
            {var subQ0=sQuery(id+"F0.wireOp",EDGE,"E21");Q2=makeQuery(id+"F3.opExtrude","CAP_EDGE",EDGE,{"disambiguationData":[OSD([subQ0]),TDD([makeQuery(id+"F0.imprint","IMPRINT",EDGE,{"disambiguationData":[TD([[makeQuery(id+"F0.imprint","INTERSECT",VERTEX,{"derivedFrom":[subQ0,sQuery(id+"F0.wireOp",EDGE,"E29")]}),-1.0]])],"derivedFrom":subQ0})])],"isStart":false});}
            var Q3;
            {var subQ0=sQuery(id+"F0.wireOp",EDGE,"E21");Q3=makeQuery(id+"F3.opExtrude","CAP_EDGE",EDGE,{"disambiguationData":[OSD([subQ0]),TDD([makeQuery(id+"F0.imprint","IMPRINT",EDGE,{"disambiguationData":[TD([[makeQuery(id+"F0.imprint","INTERSECT",VERTEX,{"derivedFrom":[sQuery(id+"F0.wireOp",EDGE,"E18.top"),subQ0]}),-1.0]])],"derivedFrom":subQ0})])],"isStart":false});}
            var Q4;
            {var subQ0=sQuery(id+"F0.wireOp",EDGE,"E21");Q4=makeQuery(id+"F3.opExtrude","CAP_EDGE",EDGE,{"disambiguationData":[OSD([subQ0]),TDD([makeQuery(id+"F0.imprint","IMPRINT",EDGE,{"disambiguationData":[TD([[makeQuery(id+"F0.imprint","INTERSECT",VERTEX,{"derivedFrom":[sQuery(id+"F0.wireOp",EDGE,"E18.bottom"),subQ0]}),1.0]])],"derivedFrom":subQ0})])],"isStart":false});}
            fillet(context, id + "F14", {"entities" : qUnion([Q0, Q1, Q2, Q3, Q4]), "radius" : 6 * mm, "allowEdgeOverflow" : false});
        }
        {
            var Q0;
            {var subQ0=sQuery(id+"F0.wireOp",EDGE,"E28");var subQ1=sQuery(id+"F0.wireOp",EDGE,"E21");var subQ2=sQuery(id+"F0.wireOp",EDGE,"E19");var subQ3=sQuery(id+"F0.wireOp",EDGE,"E18.bottom");Q0=makeQuery(id+"F12.boolean.opBoolean","MERGE",FACE,{"derivedFrom":[makeQuery(id+"F11.opExtrude","SWEPT_FACE",FACE,{"disambiguationData":[OSD([subQ3,subQ2,subQ1,subQ0])]}),makeQuery(id+"F12.opExtrude","SWEPT_FACE",FACE,{"disambiguationData":[OSD([subQ3,subQ2,subQ1,subQ0])]})]});}
            var Q1;
            {var subQ0=sQuery(id+"F0.wireOp",EDGE,"E26");var subQ1=sQuery(id+"F0.wireOp",EDGE,"E25");var subQ2=sQuery(id+"F0.wireOp",EDGE,"E21");var subQ3=sQuery(id+"F0.wireOp",EDGE,"E19");Q1=makeQuery(id+"F12.boolean.opBoolean","MERGE",FACE,{"derivedFrom":[makeQuery(id+"F11.opExtrude","SWEPT_FACE",FACE,{"disambiguationData":[OSD([subQ3,subQ2,subQ1,subQ0])]}),makeQuery(id+"F12.opExtrude","SWEPT_FACE",FACE,{"disambiguationData":[OSD([subQ3,subQ2,subQ1,subQ0])]})]});}
            var Q2;
            {var subQ0=sQuery(id+"F0.wireOp",EDGE,"E29");var subQ1=sQuery(id+"F0.wireOp",EDGE,"E23");var subQ2=sQuery(id+"F0.wireOp",EDGE,"E21");var subQ3=sQuery(id+"F0.wireOp",EDGE,"E19");Q2=makeQuery(id+"F12.boolean.opBoolean","MERGE",FACE,{"derivedFrom":[makeQuery(id+"F11.opExtrude","SWEPT_FACE",FACE,{"disambiguationData":[OSD([subQ3,subQ2,subQ1,subQ0])]}),makeQuery(id+"F12.opExtrude","SWEPT_FACE",FACE,{"disambiguationData":[OSD([subQ3,subQ2,subQ1,subQ0])]})]});}
            var Q3;
            {var subQ0=sQuery(id+"F0.wireOp",EDGE,"E31");var subQ1=sQuery(id+"F0.wireOp",EDGE,"E21");var subQ2=sQuery(id+"F0.wireOp",EDGE,"E19");var subQ3=sQuery(id+"F0.wireOp",EDGE,"E18.top");Q3=makeQuery(id+"F12.boolean.opBoolean","MERGE",FACE,{"derivedFrom":[makeQuery(id+"F11.opExtrude","SWEPT_FACE",FACE,{"disambiguationData":[OSD([subQ3,subQ2,subQ1,subQ0])]}),makeQuery(id+"F12.opExtrude","SWEPT_FACE",FACE,{"disambiguationData":[OSD([subQ3,subQ2,subQ1,subQ0])]})]});}
            extrude(context, id + "F15", {"entities" : qUnion([Q0, Q1, Q2, Q3]), "operationType" : NewBodyOperationType.ADD, "depth" : 2 * mm});
        }
        {
            var Q0;
            {var subQ0=sQuery(id+"F0.wireOp",EDGE,"E19");var subQ1=sQuery(id+"F0.wireOp",EDGE,"E18.right");var subQ2=sQuery(id+"F0.wireOp",EDGE,"E18.top");var subQ3=sQuery(id+"F0.wireOp",EDGE,"E18.bottom");var subQ4=sQuery(id+"F0.wireOp",EDGE,"E26");var subQ5=sQuery(id+"F0.wireOp",EDGE,"E25");var subQ6=sQuery(id+"F0.wireOp",EDGE,"E21");var subQ7=sQuery(id+"F0.wireOp",EDGE,"E29");var subQ8=sQuery(id+"F0.wireOp",EDGE,"E23");var subQ9=sQuery(id+"F0.wireOp",EDGE,"E31");var subQ10=sQuery(id+"F0.wireOp",EDGE,"E28");var subQ11=sQuery(id+"F0.wireOp",EDGE,"E22");Q0=makeQuery(id+"F9.opChamfer","BLEND_EDGE",EDGE,{"disambiguationData":[OD(2.0)],"blendedFrom":[makeQuery(id+"F4.opExtrude","CAP_EDGE",EDGE,{"disambiguationData":[OSD([subQ1])],"isStart":true}),makeQuery(id+"F4.boolean.opBoolean","MERGE",FACE,{"derivedFrom":[makeQuery(id+"F3.boolean.opBoolean","MERGE",FACE,{"derivedFrom":[makeQuery(id+"F2.boolean.opBoolean","MERGE",FACE,{"derivedFrom":[makeQuery(id+"F1.opExtrude","CAP_FACE",FACE,{"disambiguationData":[OSD([sQuery(id+"F0.wireOp",EDGE,"E14"),sQuery(id+"F0.wireOp",EDGE,"E15"),sQuery(id+"F0.wireOp",EDGE,"E16"),sQuery(id+"F0.wireOp",EDGE,"E17"),subQ3,subQ2,sQuery(id+"F0.wireOp",EDGE,"E18.left"),subQ11,sQuery(id+"F0.wireOp",EDGE,"E34"),sQuery(id+"F0.wireOp",EDGE,"E35"),sQuery(id+"F0.wireOp",EDGE,"E36"),sQuery(id+"F0.wireOp",EDGE,"E37"),sQuery(id+"F0.wireOp",EDGE,"E38.bottom"),sQuery(id+"F0.wireOp",EDGE,"E38.top"),sQuery(id+"F0.wireOp",EDGE,"E38.left"),sQuery(id+"F0.wireOp",EDGE,"E38.right"),sQuery(id+"F0.wireOp",EDGE,"E39.bottom"),sQuery(id+"F0.wireOp",EDGE,"E39.top"),sQuery(id+"F0.wireOp",EDGE,"E39.left"),sQuery(id+"F0.wireOp",EDGE,"E39.right"),sQuery(id+"F0.wireOp",EDGE,"dDL4M1PI-aelY-u7zt-lnq0-sMzwrNtlq2yo"),sQuery(id+"F0.wireOp",EDGE,"E40")])],"isStart":true}),makeQuery(id+"F2.opExtrude","CAP_FACE",FACE,{"disambiguationData":[OSD([subQ3,subQ2,subQ6,subQ11,subQ8,sQuery(id+"F0.wireOp",EDGE,"E24"),subQ5,subQ4,sQuery(id+"F0.wireOp",EDGE,"E27"),subQ10,subQ7,sQuery(id+"F0.wireOp",EDGE,"E30"),subQ9])],"isStart":true})]}),makeQuery(id+"F3.opExtrude","CAP_FACE",FACE,{"disambiguationData":[OSD([subQ3,subQ0,subQ6,subQ10])],"isStart":true}),makeQuery(id+"F3.opExtrude","CAP_FACE",FACE,{"disambiguationData":[OSD([subQ2,subQ0,subQ6,subQ9])],"isStart":true}),makeQuery(id+"F3.opExtrude","CAP_FACE",FACE,{"disambiguationData":[OSD([subQ0,subQ6,subQ8,subQ7])],"isStart":true}),makeQuery(id+"F3.opExtrude","CAP_FACE",FACE,{"disambiguationData":[OSD([subQ0,subQ6,subQ5,subQ4])],"isStart":true})]}),makeQuery(id+"F4.opExtrude","CAP_FACE",FACE,{"disambiguationData":[OSD([subQ3,subQ2,subQ1,subQ0])],"isStart":true})]})],"blendedInto":[makeQuery(id+"F4.boolean.opBoolean","MERGE",FACE,{"derivedFrom":[makeQuery(id+"F3.boolean.opBoolean","MERGE",FACE,{"derivedFrom":[makeQuery(id+"F2.boolean.opBoolean","MERGE",FACE,{"derivedFrom":[makeQuery(id+"F1.opExtrude","CAP_FACE",FACE,{"disambiguationData":[OSD([sQuery(id+"F0.wireOp",EDGE,"E14"),sQuery(id+"F0.wireOp",EDGE,"E15"),sQuery(id+"F0.wireOp",EDGE,"E16"),sQuery(id+"F0.wireOp",EDGE,"E17"),subQ3,subQ2,sQuery(id+"F0.wireOp",EDGE,"E18.left"),subQ11,sQuery(id+"F0.wireOp",EDGE,"E34"),sQuery(id+"F0.wireOp",EDGE,"E35"),sQuery(id+"F0.wireOp",EDGE,"E36"),sQuery(id+"F0.wireOp",EDGE,"E37"),sQuery(id+"F0.wireOp",EDGE,"E38.bottom"),sQuery(id+"F0.wireOp",EDGE,"E38.top"),sQuery(id+"F0.wireOp",EDGE,"E38.left"),sQuery(id+"F0.wireOp",EDGE,"E38.right"),sQuery(id+"F0.wireOp",EDGE,"E39.bottom"),sQuery(id+"F0.wireOp",EDGE,"E39.top"),sQuery(id+"F0.wireOp",EDGE,"E39.left"),sQuery(id+"F0.wireOp",EDGE,"E39.right"),sQuery(id+"F0.wireOp",EDGE,"dDL4M1PI-aelY-u7zt-lnq0-sMzwrNtlq2yo"),sQuery(id+"F0.wireOp",EDGE,"E40")])],"isStart":true}),makeQuery(id+"F2.opExtrude","CAP_FACE",FACE,{"disambiguationData":[OSD([subQ3,subQ2,subQ6,subQ11,subQ8,sQuery(id+"F0.wireOp",EDGE,"E24"),subQ5,subQ4,sQuery(id+"F0.wireOp",EDGE,"E27"),subQ10,subQ7,sQuery(id+"F0.wireOp",EDGE,"E30"),subQ9])],"isStart":true})]}),makeQuery(id+"F3.opExtrude","CAP_FACE",FACE,{"disambiguationData":[OSD([subQ3,subQ0,subQ6,subQ10])],"isStart":true}),makeQuery(id+"F3.opExtrude","CAP_FACE",FACE,{"disambiguationData":[OSD([subQ2,subQ0,subQ6,subQ9])],"isStart":true}),makeQuery(id+"F3.opExtrude","CAP_FACE",FACE,{"disambiguationData":[OSD([subQ0,subQ6,subQ8,subQ7])],"isStart":true}),makeQuery(id+"F3.opExtrude","CAP_FACE",FACE,{"disambiguationData":[OSD([subQ0,subQ6,subQ5,subQ4])],"isStart":true})]}),makeQuery(id+"F4.opExtrude","CAP_FACE",FACE,{"disambiguationData":[OSD([subQ3,subQ2,subQ1,subQ0])],"isStart":true})]})]});}
            var Q1;
            {var subQ0=sQuery(id+"F0.wireOp",EDGE,"E19");var subQ1=sQuery(id+"F0.wireOp",EDGE,"E18.right");var subQ2=sQuery(id+"F0.wireOp",EDGE,"E18.top");var subQ3=sQuery(id+"F0.wireOp",EDGE,"E18.bottom");var subQ4=sQuery(id+"F0.wireOp",EDGE,"E26");var subQ5=sQuery(id+"F0.wireOp",EDGE,"E25");var subQ6=sQuery(id+"F0.wireOp",EDGE,"E21");var subQ7=sQuery(id+"F0.wireOp",EDGE,"E29");var subQ8=sQuery(id+"F0.wireOp",EDGE,"E23");var subQ9=sQuery(id+"F0.wireOp",EDGE,"E31");var subQ10=sQuery(id+"F0.wireOp",EDGE,"E28");var subQ11=sQuery(id+"F0.wireOp",EDGE,"E22");Q1=makeQuery(id+"F9.opChamfer","BLEND_EDGE",EDGE,{"disambiguationData":[OD(1.0)],"blendedFrom":[makeQuery(id+"F4.opExtrude","CAP_EDGE",EDGE,{"disambiguationData":[OSD([subQ1])],"isStart":true}),makeQuery(id+"F4.boolean.opBoolean","MERGE",FACE,{"derivedFrom":[makeQuery(id+"F3.boolean.opBoolean","MERGE",FACE,{"derivedFrom":[makeQuery(id+"F2.boolean.opBoolean","MERGE",FACE,{"derivedFrom":[makeQuery(id+"F1.opExtrude","CAP_FACE",FACE,{"disambiguationData":[OSD([sQuery(id+"F0.wireOp",EDGE,"E14"),sQuery(id+"F0.wireOp",EDGE,"E15"),sQuery(id+"F0.wireOp",EDGE,"E16"),sQuery(id+"F0.wireOp",EDGE,"E17"),subQ3,subQ2,sQuery(id+"F0.wireOp",EDGE,"E18.left"),subQ11,sQuery(id+"F0.wireOp",EDGE,"E34"),sQuery(id+"F0.wireOp",EDGE,"E35"),sQuery(id+"F0.wireOp",EDGE,"E36"),sQuery(id+"F0.wireOp",EDGE,"E37"),sQuery(id+"F0.wireOp",EDGE,"E38.bottom"),sQuery(id+"F0.wireOp",EDGE,"E38.top"),sQuery(id+"F0.wireOp",EDGE,"E38.left"),sQuery(id+"F0.wireOp",EDGE,"E38.right"),sQuery(id+"F0.wireOp",EDGE,"E39.bottom"),sQuery(id+"F0.wireOp",EDGE,"E39.top"),sQuery(id+"F0.wireOp",EDGE,"E39.left"),sQuery(id+"F0.wireOp",EDGE,"E39.right"),sQuery(id+"F0.wireOp",EDGE,"dDL4M1PI-aelY-u7zt-lnq0-sMzwrNtlq2yo"),sQuery(id+"F0.wireOp",EDGE,"E40")])],"isStart":true}),makeQuery(id+"F2.opExtrude","CAP_FACE",FACE,{"disambiguationData":[OSD([subQ3,subQ2,subQ6,subQ11,subQ8,sQuery(id+"F0.wireOp",EDGE,"E24"),subQ5,subQ4,sQuery(id+"F0.wireOp",EDGE,"E27"),subQ10,subQ7,sQuery(id+"F0.wireOp",EDGE,"E30"),subQ9])],"isStart":true})]}),makeQuery(id+"F3.opExtrude","CAP_FACE",FACE,{"disambiguationData":[OSD([subQ3,subQ0,subQ6,subQ10])],"isStart":true}),makeQuery(id+"F3.opExtrude","CAP_FACE",FACE,{"disambiguationData":[OSD([subQ2,subQ0,subQ6,subQ9])],"isStart":true}),makeQuery(id+"F3.opExtrude","CAP_FACE",FACE,{"disambiguationData":[OSD([subQ0,subQ6,subQ8,subQ7])],"isStart":true}),makeQuery(id+"F3.opExtrude","CAP_FACE",FACE,{"disambiguationData":[OSD([subQ0,subQ6,subQ5,subQ4])],"isStart":true})]}),makeQuery(id+"F4.opExtrude","CAP_FACE",FACE,{"disambiguationData":[OSD([subQ3,subQ2,subQ1,subQ0])],"isStart":true})]})],"blendedInto":[makeQuery(id+"F4.boolean.opBoolean","MERGE",FACE,{"derivedFrom":[makeQuery(id+"F3.boolean.opBoolean","MERGE",FACE,{"derivedFrom":[makeQuery(id+"F2.boolean.opBoolean","MERGE",FACE,{"derivedFrom":[makeQuery(id+"F1.opExtrude","CAP_FACE",FACE,{"disambiguationData":[OSD([sQuery(id+"F0.wireOp",EDGE,"E14"),sQuery(id+"F0.wireOp",EDGE,"E15"),sQuery(id+"F0.wireOp",EDGE,"E16"),sQuery(id+"F0.wireOp",EDGE,"E17"),subQ3,subQ2,sQuery(id+"F0.wireOp",EDGE,"E18.left"),subQ11,sQuery(id+"F0.wireOp",EDGE,"E34"),sQuery(id+"F0.wireOp",EDGE,"E35"),sQuery(id+"F0.wireOp",EDGE,"E36"),sQuery(id+"F0.wireOp",EDGE,"E37"),sQuery(id+"F0.wireOp",EDGE,"E38.bottom"),sQuery(id+"F0.wireOp",EDGE,"E38.top"),sQuery(id+"F0.wireOp",EDGE,"E38.left"),sQuery(id+"F0.wireOp",EDGE,"E38.right"),sQuery(id+"F0.wireOp",EDGE,"E39.bottom"),sQuery(id+"F0.wireOp",EDGE,"E39.top"),sQuery(id+"F0.wireOp",EDGE,"E39.left"),sQuery(id+"F0.wireOp",EDGE,"E39.right"),sQuery(id+"F0.wireOp",EDGE,"dDL4M1PI-aelY-u7zt-lnq0-sMzwrNtlq2yo"),sQuery(id+"F0.wireOp",EDGE,"E40")])],"isStart":true}),makeQuery(id+"F2.opExtrude","CAP_FACE",FACE,{"disambiguationData":[OSD([subQ3,subQ2,subQ6,subQ11,subQ8,sQuery(id+"F0.wireOp",EDGE,"E24"),subQ5,subQ4,sQuery(id+"F0.wireOp",EDGE,"E27"),subQ10,subQ7,sQuery(id+"F0.wireOp",EDGE,"E30"),subQ9])],"isStart":true})]}),makeQuery(id+"F3.opExtrude","CAP_FACE",FACE,{"disambiguationData":[OSD([subQ3,subQ0,subQ6,subQ10])],"isStart":true}),makeQuery(id+"F3.opExtrude","CAP_FACE",FACE,{"disambiguationData":[OSD([subQ2,subQ0,subQ6,subQ9])],"isStart":true}),makeQuery(id+"F3.opExtrude","CAP_FACE",FACE,{"disambiguationData":[OSD([subQ0,subQ6,subQ8,subQ7])],"isStart":true}),makeQuery(id+"F3.opExtrude","CAP_FACE",FACE,{"disambiguationData":[OSD([subQ0,subQ6,subQ5,subQ4])],"isStart":true})]}),makeQuery(id+"F4.opExtrude","CAP_FACE",FACE,{"disambiguationData":[OSD([subQ3,subQ2,subQ1,subQ0])],"isStart":true})]})]});}
            var Q2;
            {var subQ0=sQuery(id+"F0.wireOp",EDGE,"E19");var subQ1=sQuery(id+"F0.wireOp",EDGE,"E18.right");var subQ2=sQuery(id+"F0.wireOp",EDGE,"E18.top");var subQ3=sQuery(id+"F0.wireOp",EDGE,"E18.bottom");var subQ4=sQuery(id+"F0.wireOp",EDGE,"E26");var subQ5=sQuery(id+"F0.wireOp",EDGE,"E25");var subQ6=sQuery(id+"F0.wireOp",EDGE,"E21");var subQ7=sQuery(id+"F0.wireOp",EDGE,"E29");var subQ8=sQuery(id+"F0.wireOp",EDGE,"E23");var subQ9=sQuery(id+"F0.wireOp",EDGE,"E31");var subQ10=sQuery(id+"F0.wireOp",EDGE,"E28");var subQ11=sQuery(id+"F0.wireOp",EDGE,"E22");Q2=makeQuery(id+"F9.opChamfer","BLEND_EDGE",EDGE,{"disambiguationData":[OD(0.0)],"blendedFrom":[makeQuery(id+"F4.opExtrude","CAP_EDGE",EDGE,{"disambiguationData":[OSD([subQ1])],"isStart":true}),makeQuery(id+"F4.boolean.opBoolean","MERGE",FACE,{"derivedFrom":[makeQuery(id+"F3.boolean.opBoolean","MERGE",FACE,{"derivedFrom":[makeQuery(id+"F2.boolean.opBoolean","MERGE",FACE,{"derivedFrom":[makeQuery(id+"F1.opExtrude","CAP_FACE",FACE,{"disambiguationData":[OSD([sQuery(id+"F0.wireOp",EDGE,"E14"),sQuery(id+"F0.wireOp",EDGE,"E15"),sQuery(id+"F0.wireOp",EDGE,"E16"),sQuery(id+"F0.wireOp",EDGE,"E17"),subQ3,subQ2,sQuery(id+"F0.wireOp",EDGE,"E18.left"),subQ11,sQuery(id+"F0.wireOp",EDGE,"E34"),sQuery(id+"F0.wireOp",EDGE,"E35"),sQuery(id+"F0.wireOp",EDGE,"E36"),sQuery(id+"F0.wireOp",EDGE,"E37"),sQuery(id+"F0.wireOp",EDGE,"E38.bottom"),sQuery(id+"F0.wireOp",EDGE,"E38.top"),sQuery(id+"F0.wireOp",EDGE,"E38.left"),sQuery(id+"F0.wireOp",EDGE,"E38.right"),sQuery(id+"F0.wireOp",EDGE,"E39.bottom"),sQuery(id+"F0.wireOp",EDGE,"E39.top"),sQuery(id+"F0.wireOp",EDGE,"E39.left"),sQuery(id+"F0.wireOp",EDGE,"E39.right"),sQuery(id+"F0.wireOp",EDGE,"dDL4M1PI-aelY-u7zt-lnq0-sMzwrNtlq2yo"),sQuery(id+"F0.wireOp",EDGE,"E40")])],"isStart":true}),makeQuery(id+"F2.opExtrude","CAP_FACE",FACE,{"disambiguationData":[OSD([subQ3,subQ2,subQ6,subQ11,subQ8,sQuery(id+"F0.wireOp",EDGE,"E24"),subQ5,subQ4,sQuery(id+"F0.wireOp",EDGE,"E27"),subQ10,subQ7,sQuery(id+"F0.wireOp",EDGE,"E30"),subQ9])],"isStart":true})]}),makeQuery(id+"F3.opExtrude","CAP_FACE",FACE,{"disambiguationData":[OSD([subQ3,subQ0,subQ6,subQ10])],"isStart":true}),makeQuery(id+"F3.opExtrude","CAP_FACE",FACE,{"disambiguationData":[OSD([subQ2,subQ0,subQ6,subQ9])],"isStart":true}),makeQuery(id+"F3.opExtrude","CAP_FACE",FACE,{"disambiguationData":[OSD([subQ0,subQ6,subQ8,subQ7])],"isStart":true}),makeQuery(id+"F3.opExtrude","CAP_FACE",FACE,{"disambiguationData":[OSD([subQ0,subQ6,subQ5,subQ4])],"isStart":true})]}),makeQuery(id+"F4.opExtrude","CAP_FACE",FACE,{"disambiguationData":[OSD([subQ3,subQ2,subQ1,subQ0])],"isStart":true})]})],"blendedInto":[makeQuery(id+"F4.boolean.opBoolean","MERGE",FACE,{"derivedFrom":[makeQuery(id+"F3.boolean.opBoolean","MERGE",FACE,{"derivedFrom":[makeQuery(id+"F2.boolean.opBoolean","MERGE",FACE,{"derivedFrom":[makeQuery(id+"F1.opExtrude","CAP_FACE",FACE,{"disambiguationData":[OSD([sQuery(id+"F0.wireOp",EDGE,"E14"),sQuery(id+"F0.wireOp",EDGE,"E15"),sQuery(id+"F0.wireOp",EDGE,"E16"),sQuery(id+"F0.wireOp",EDGE,"E17"),subQ3,subQ2,sQuery(id+"F0.wireOp",EDGE,"E18.left"),subQ11,sQuery(id+"F0.wireOp",EDGE,"E34"),sQuery(id+"F0.wireOp",EDGE,"E35"),sQuery(id+"F0.wireOp",EDGE,"E36"),sQuery(id+"F0.wireOp",EDGE,"E37"),sQuery(id+"F0.wireOp",EDGE,"E38.bottom"),sQuery(id+"F0.wireOp",EDGE,"E38.top"),sQuery(id+"F0.wireOp",EDGE,"E38.left"),sQuery(id+"F0.wireOp",EDGE,"E38.right"),sQuery(id+"F0.wireOp",EDGE,"E39.bottom"),sQuery(id+"F0.wireOp",EDGE,"E39.top"),sQuery(id+"F0.wireOp",EDGE,"E39.left"),sQuery(id+"F0.wireOp",EDGE,"E39.right"),sQuery(id+"F0.wireOp",EDGE,"dDL4M1PI-aelY-u7zt-lnq0-sMzwrNtlq2yo"),sQuery(id+"F0.wireOp",EDGE,"E40")])],"isStart":true}),makeQuery(id+"F2.opExtrude","CAP_FACE",FACE,{"disambiguationData":[OSD([subQ3,subQ2,subQ6,subQ11,subQ8,sQuery(id+"F0.wireOp",EDGE,"E24"),subQ5,subQ4,sQuery(id+"F0.wireOp",EDGE,"E27"),subQ10,subQ7,sQuery(id+"F0.wireOp",EDGE,"E30"),subQ9])],"isStart":true})]}),makeQuery(id+"F3.opExtrude","CAP_FACE",FACE,{"disambiguationData":[OSD([subQ3,subQ0,subQ6,subQ10])],"isStart":true}),makeQuery(id+"F3.opExtrude","CAP_FACE",FACE,{"disambiguationData":[OSD([subQ2,subQ0,subQ6,subQ9])],"isStart":true}),makeQuery(id+"F3.opExtrude","CAP_FACE",FACE,{"disambiguationData":[OSD([subQ0,subQ6,subQ8,subQ7])],"isStart":true}),makeQuery(id+"F3.opExtrude","CAP_FACE",FACE,{"disambiguationData":[OSD([subQ0,subQ6,subQ5,subQ4])],"isStart":true})]}),makeQuery(id+"F4.opExtrude","CAP_FACE",FACE,{"disambiguationData":[OSD([subQ3,subQ2,subQ1,subQ0])],"isStart":true})]})]});}
            var Q3;
            {var subQ0=sQuery(id+"F0.wireOp",EDGE,"E19");var subQ1=sQuery(id+"F0.wireOp",EDGE,"E18.right");var subQ2=sQuery(id+"F0.wireOp",EDGE,"E18.top");var subQ3=sQuery(id+"F0.wireOp",EDGE,"E18.bottom");var subQ4=sQuery(id+"F0.wireOp",EDGE,"E26");var subQ5=sQuery(id+"F0.wireOp",EDGE,"E25");var subQ6=sQuery(id+"F0.wireOp",EDGE,"E21");var subQ7=sQuery(id+"F0.wireOp",EDGE,"E29");var subQ8=sQuery(id+"F0.wireOp",EDGE,"E23");var subQ9=sQuery(id+"F0.wireOp",EDGE,"E31");var subQ10=sQuery(id+"F0.wireOp",EDGE,"E28");var subQ11=sQuery(id+"F0.wireOp",EDGE,"E22");Q3=makeQuery(id+"F9.opChamfer","BLEND_EDGE",EDGE,{"disambiguationData":[OD(3.0)],"blendedFrom":[makeQuery(id+"F4.opExtrude","CAP_EDGE",EDGE,{"disambiguationData":[OSD([subQ1])],"isStart":true}),makeQuery(id+"F4.boolean.opBoolean","MERGE",FACE,{"derivedFrom":[makeQuery(id+"F3.boolean.opBoolean","MERGE",FACE,{"derivedFrom":[makeQuery(id+"F2.boolean.opBoolean","MERGE",FACE,{"derivedFrom":[makeQuery(id+"F1.opExtrude","CAP_FACE",FACE,{"disambiguationData":[OSD([sQuery(id+"F0.wireOp",EDGE,"E14"),sQuery(id+"F0.wireOp",EDGE,"E15"),sQuery(id+"F0.wireOp",EDGE,"E16"),sQuery(id+"F0.wireOp",EDGE,"E17"),subQ3,subQ2,sQuery(id+"F0.wireOp",EDGE,"E18.left"),subQ11,sQuery(id+"F0.wireOp",EDGE,"E34"),sQuery(id+"F0.wireOp",EDGE,"E35"),sQuery(id+"F0.wireOp",EDGE,"E36"),sQuery(id+"F0.wireOp",EDGE,"E37"),sQuery(id+"F0.wireOp",EDGE,"E38.bottom"),sQuery(id+"F0.wireOp",EDGE,"E38.top"),sQuery(id+"F0.wireOp",EDGE,"E38.left"),sQuery(id+"F0.wireOp",EDGE,"E38.right"),sQuery(id+"F0.wireOp",EDGE,"E39.bottom"),sQuery(id+"F0.wireOp",EDGE,"E39.top"),sQuery(id+"F0.wireOp",EDGE,"E39.left"),sQuery(id+"F0.wireOp",EDGE,"E39.right"),sQuery(id+"F0.wireOp",EDGE,"dDL4M1PI-aelY-u7zt-lnq0-sMzwrNtlq2yo"),sQuery(id+"F0.wireOp",EDGE,"E40")])],"isStart":true}),makeQuery(id+"F2.opExtrude","CAP_FACE",FACE,{"disambiguationData":[OSD([subQ3,subQ2,subQ6,subQ11,subQ8,sQuery(id+"F0.wireOp",EDGE,"E24"),subQ5,subQ4,sQuery(id+"F0.wireOp",EDGE,"E27"),subQ10,subQ7,sQuery(id+"F0.wireOp",EDGE,"E30"),subQ9])],"isStart":true})]}),makeQuery(id+"F3.opExtrude","CAP_FACE",FACE,{"disambiguationData":[OSD([subQ3,subQ0,subQ6,subQ10])],"isStart":true}),makeQuery(id+"F3.opExtrude","CAP_FACE",FACE,{"disambiguationData":[OSD([subQ2,subQ0,subQ6,subQ9])],"isStart":true}),makeQuery(id+"F3.opExtrude","CAP_FACE",FACE,{"disambiguationData":[OSD([subQ0,subQ6,subQ8,subQ7])],"isStart":true}),makeQuery(id+"F3.opExtrude","CAP_FACE",FACE,{"disambiguationData":[OSD([subQ0,subQ6,subQ5,subQ4])],"isStart":true})]}),makeQuery(id+"F4.opExtrude","CAP_FACE",FACE,{"disambiguationData":[OSD([subQ3,subQ2,subQ1,subQ0])],"isStart":true})]})],"blendedInto":[makeQuery(id+"F4.boolean.opBoolean","MERGE",FACE,{"derivedFrom":[makeQuery(id+"F3.boolean.opBoolean","MERGE",FACE,{"derivedFrom":[makeQuery(id+"F2.boolean.opBoolean","MERGE",FACE,{"derivedFrom":[makeQuery(id+"F1.opExtrude","CAP_FACE",FACE,{"disambiguationData":[OSD([sQuery(id+"F0.wireOp",EDGE,"E14"),sQuery(id+"F0.wireOp",EDGE,"E15"),sQuery(id+"F0.wireOp",EDGE,"E16"),sQuery(id+"F0.wireOp",EDGE,"E17"),subQ3,subQ2,sQuery(id+"F0.wireOp",EDGE,"E18.left"),subQ11,sQuery(id+"F0.wireOp",EDGE,"E34"),sQuery(id+"F0.wireOp",EDGE,"E35"),sQuery(id+"F0.wireOp",EDGE,"E36"),sQuery(id+"F0.wireOp",EDGE,"E37"),sQuery(id+"F0.wireOp",EDGE,"E38.bottom"),sQuery(id+"F0.wireOp",EDGE,"E38.top"),sQuery(id+"F0.wireOp",EDGE,"E38.left"),sQuery(id+"F0.wireOp",EDGE,"E38.right"),sQuery(id+"F0.wireOp",EDGE,"E39.bottom"),sQuery(id+"F0.wireOp",EDGE,"E39.top"),sQuery(id+"F0.wireOp",EDGE,"E39.left"),sQuery(id+"F0.wireOp",EDGE,"E39.right"),sQuery(id+"F0.wireOp",EDGE,"dDL4M1PI-aelY-u7zt-lnq0-sMzwrNtlq2yo"),sQuery(id+"F0.wireOp",EDGE,"E40")])],"isStart":true}),makeQuery(id+"F2.opExtrude","CAP_FACE",FACE,{"disambiguationData":[OSD([subQ3,subQ2,subQ6,subQ11,subQ8,sQuery(id+"F0.wireOp",EDGE,"E24"),subQ5,subQ4,sQuery(id+"F0.wireOp",EDGE,"E27"),subQ10,subQ7,sQuery(id+"F0.wireOp",EDGE,"E30"),subQ9])],"isStart":true})]}),makeQuery(id+"F3.opExtrude","CAP_FACE",FACE,{"disambiguationData":[OSD([subQ3,subQ0,subQ6,subQ10])],"isStart":true}),makeQuery(id+"F3.opExtrude","CAP_FACE",FACE,{"disambiguationData":[OSD([subQ2,subQ0,subQ6,subQ9])],"isStart":true}),makeQuery(id+"F3.opExtrude","CAP_FACE",FACE,{"disambiguationData":[OSD([subQ0,subQ6,subQ8,subQ7])],"isStart":true}),makeQuery(id+"F3.opExtrude","CAP_FACE",FACE,{"disambiguationData":[OSD([subQ0,subQ6,subQ5,subQ4])],"isStart":true})]}),makeQuery(id+"F4.opExtrude","CAP_FACE",FACE,{"disambiguationData":[OSD([subQ3,subQ2,subQ1,subQ0])],"isStart":true})]})]});}
            fillet(context, id + "F16", {"entities" : qUnion([Q0, Q1, Q2, Q3]), "radius" : 5 * mm, "tangentPropagation" : true, "allowEdgeOverflow" : false});
        }
        {
            var Q0;
            {var subQ0=sQuery(id+"F0.wireOp",EDGE,"E28");var subQ1=sQuery(id+"F0.wireOp",EDGE,"E21");var subQ2=sQuery(id+"F0.wireOp",EDGE,"E19");var subQ3=sQuery(id+"F0.wireOp",EDGE,"E18.bottom");Q0=makeQuery(id+"F15.opExtrude","CAP_EDGE",EDGE,{"disambiguationData":[OSD([subQ3,subQ2,subQ1,subQ0]),TDD([makeQuery(id+"F11.boolean.opBoolean","MERGE",EDGE,{"derivedFrom":[makeQuery(id+"F10.opChamfer","BLEND_EDGE",EDGE,{"blendedFrom":[makeQuery(id+"F3.opExtrude","CAP_EDGE",EDGE,{"disambiguationData":[OSD([subQ2]),TDD([makeQuery(id+"F0.imprint","IMPRINT",EDGE,{"disambiguationData":[TD([[makeQuery(id+"F0.imprint","INTERSECT",VERTEX,{"derivedFrom":[subQ3,subQ2]}),1.0]])],"derivedFrom":subQ2})])],"isStart":false}),makeQuery(id+"F3.opExtrude","CAP_FACE",FACE,{"disambiguationData":[OSD([subQ3,subQ2,subQ1,subQ0])],"isStart":false})],"blendedInto":[makeQuery(id+"F3.opExtrude","CAP_FACE",FACE,{"disambiguationData":[OSD([subQ3,subQ2,subQ1,subQ0])],"isStart":false})]}),makeQuery(id+"F11.opExtrude","CAP_EDGE",EDGE,{"disambiguationData":[OSD([subQ3,subQ2,subQ1,subQ0])],"isStart":true})]})])],"isStart":false});}
            var Q1;
            {var subQ0=sQuery(id+"F0.wireOp",EDGE,"E26");var subQ1=sQuery(id+"F0.wireOp",EDGE,"E25");var subQ2=sQuery(id+"F0.wireOp",EDGE,"E21");var subQ3=sQuery(id+"F0.wireOp",EDGE,"E19");Q1=makeQuery(id+"F15.opExtrude","CAP_EDGE",EDGE,{"disambiguationData":[OSD([subQ3,subQ2,subQ1,subQ0]),TDD([makeQuery(id+"F11.boolean.opBoolean","MERGE",EDGE,{"derivedFrom":[makeQuery(id+"F10.opChamfer","BLEND_EDGE",EDGE,{"blendedFrom":[makeQuery(id+"F3.opExtrude","CAP_EDGE",EDGE,{"disambiguationData":[OSD([subQ3]),TDD([makeQuery(id+"F0.imprint","IMPRINT",EDGE,{"disambiguationData":[TD([[makeQuery(id+"F0.imprint","INTERSECT",VERTEX,{"derivedFrom":[subQ3,subQ1]}),-1.0]])],"derivedFrom":subQ3})])],"isStart":false}),makeQuery(id+"F3.opExtrude","CAP_FACE",FACE,{"disambiguationData":[OSD([subQ3,subQ2,subQ1,subQ0])],"isStart":false})],"blendedInto":[makeQuery(id+"F3.opExtrude","CAP_FACE",FACE,{"disambiguationData":[OSD([subQ3,subQ2,subQ1,subQ0])],"isStart":false})]}),makeQuery(id+"F11.opExtrude","CAP_EDGE",EDGE,{"disambiguationData":[OSD([subQ3,subQ2,subQ1,subQ0])],"isStart":true})]})])],"isStart":false});}
            var Q2;
            {var subQ0=sQuery(id+"F0.wireOp",EDGE,"E29");var subQ1=sQuery(id+"F0.wireOp",EDGE,"E23");var subQ2=sQuery(id+"F0.wireOp",EDGE,"E21");var subQ3=sQuery(id+"F0.wireOp",EDGE,"E19");Q2=makeQuery(id+"F15.opExtrude","CAP_EDGE",EDGE,{"disambiguationData":[OSD([subQ3,subQ2,subQ1,subQ0]),TDD([makeQuery(id+"F11.boolean.opBoolean","MERGE",EDGE,{"derivedFrom":[makeQuery(id+"F10.opChamfer","BLEND_EDGE",EDGE,{"blendedFrom":[makeQuery(id+"F3.opExtrude","CAP_EDGE",EDGE,{"disambiguationData":[OSD([subQ3]),TDD([makeQuery(id+"F0.imprint","IMPRINT",EDGE,{"disambiguationData":[TD([[makeQuery(id+"F0.imprint","INTERSECT",VERTEX,{"derivedFrom":[subQ3,subQ0]}),-1.0]])],"derivedFrom":subQ3})])],"isStart":false}),makeQuery(id+"F3.opExtrude","CAP_FACE",FACE,{"disambiguationData":[OSD([subQ3,subQ2,subQ1,subQ0])],"isStart":false})],"blendedInto":[makeQuery(id+"F3.opExtrude","CAP_FACE",FACE,{"disambiguationData":[OSD([subQ3,subQ2,subQ1,subQ0])],"isStart":false})]}),makeQuery(id+"F11.opExtrude","CAP_EDGE",EDGE,{"disambiguationData":[OSD([subQ3,subQ2,subQ1,subQ0])],"isStart":true})]})])],"isStart":false});}
            var Q3;
            {var subQ0=sQuery(id+"F0.wireOp",EDGE,"E31");var subQ1=sQuery(id+"F0.wireOp",EDGE,"E21");var subQ2=sQuery(id+"F0.wireOp",EDGE,"E19");var subQ3=sQuery(id+"F0.wireOp",EDGE,"E18.top");Q3=makeQuery(id+"F15.opExtrude","CAP_EDGE",EDGE,{"disambiguationData":[OSD([subQ3,subQ2,subQ1,subQ0]),TDD([makeQuery(id+"F11.boolean.opBoolean","MERGE",EDGE,{"derivedFrom":[makeQuery(id+"F10.opChamfer","BLEND_EDGE",EDGE,{"blendedFrom":[makeQuery(id+"F3.opExtrude","CAP_EDGE",EDGE,{"disambiguationData":[OSD([subQ2]),TDD([makeQuery(id+"F0.imprint","IMPRINT",EDGE,{"disambiguationData":[TD([[makeQuery(id+"F0.imprint","INTERSECT",VERTEX,{"derivedFrom":[subQ3,subQ2]}),-1.0]])],"derivedFrom":subQ2})])],"isStart":false}),makeQuery(id+"F3.opExtrude","CAP_FACE",FACE,{"disambiguationData":[OSD([subQ3,subQ2,subQ1,subQ0])],"isStart":false})],"blendedInto":[makeQuery(id+"F3.opExtrude","CAP_FACE",FACE,{"disambiguationData":[OSD([subQ3,subQ2,subQ1,subQ0])],"isStart":false})]}),makeQuery(id+"F11.opExtrude","CAP_EDGE",EDGE,{"disambiguationData":[OSD([subQ3,subQ2,subQ1,subQ0])],"isStart":true})]})])],"isStart":false});}
            chamfer(context, id + "F17", {"entities" : qUnion([Q0, Q1, Q2, Q3]), "chamferType" : ChamferType.TWO_OFFSETS, "width1" : 2 * mm, "oppositeDirection" : false, "width2" : 10 * mm, "tangentPropagation" : true});
        }
        {
            var Q0;
            {var subQ0=sQuery(id+"F0.wireOp",EDGE,"E18.bottom");var subQ2=sQuery(id+"F0.wireOp",EDGE,"E19");var subQ3=makeQuery(id+"F0.imprint","IMPRINT",EDGE,{"disambiguationData":[TD([[makeQuery(id+"F0.imprint","INTERSECT",VERTEX,{"derivedFrom":[subQ0,subQ2]}),1.0]])],"derivedFrom":subQ2});var subQ4=sQuery(id+"F5.wireOp",EDGE,"E54.top");Q0=makeQuery(id+"F13.opChamfer","BLEND_FACE",FACE,{"disambiguationData":[OSD([subQ2,subQ4]),TDD([makeQuery(id+"F12.opExtrude","CAP_EDGE",EDGE,{"disambiguationData":[OSD([subQ2,subQ4]),TDD([makeQuery(id+"F11.opExtrude","CAP_EDGE",EDGE,{"disambiguationData":[OSD([subQ2,subQ4]),TDD([makeQuery(id+"F10.opChamfer","BLEND_EDGE",EDGE,{"blendedFrom":[makeQuery(id+"F3.opExtrude","CAP_EDGE",EDGE,{"disambiguationData":[OSD([subQ2]),TDD([subQ3])],"isStart":false}),makeQuery(id+"F6.boolean.opBoolean","COPY",FACE,{"disambiguationData":[TD([makeQuery(id+"F2.opExtrude","SWEPT_FACE",FACE,{"disambiguationData":[OSD([subQ0])]})])],"derivedFrom":makeQuery(id+"F6.opExtrude","SWEPT_FACE",FACE,{"disambiguationData":[OSD([subQ4])]})})],"blendedInto":[makeQuery(id+"F6.boolean.opBoolean","COPY",FACE,{"disambiguationData":[TD([makeQuery(id+"F2.opExtrude","SWEPT_FACE",FACE,{"disambiguationData":[OSD([subQ0])]})])],"derivedFrom":makeQuery(id+"F6.opExtrude","SWEPT_FACE",FACE,{"disambiguationData":[OSD([subQ4])]})})]})])],"isStart":false})])],"isStart":false})])]});}
            var Q1;
            {var subQ0=sQuery(id+"F0.wireOp",EDGE,"E25");var subQ1=sQuery(id+"F0.wireOp",EDGE,"E19");var subQ3=makeQuery(id+"F0.imprint","IMPRINT",EDGE,{"disambiguationData":[TD([[makeQuery(id+"F0.imprint","INTERSECT",VERTEX,{"derivedFrom":[subQ1,subQ0]}),-1.0]])],"derivedFrom":subQ1});var subQ4=sQuery(id+"F5.wireOp",EDGE,"E54.top");Q1=makeQuery(id+"F13.opChamfer","BLEND_FACE",FACE,{"disambiguationData":[OSD([subQ1,subQ4]),TDD([makeQuery(id+"F12.opExtrude","CAP_EDGE",EDGE,{"disambiguationData":[OSD([subQ1,subQ4]),TDD([makeQuery(id+"F11.opExtrude","CAP_EDGE",EDGE,{"disambiguationData":[OSD([subQ1,subQ4]),TDD([makeQuery(id+"F10.opChamfer","BLEND_EDGE",EDGE,{"blendedFrom":[makeQuery(id+"F3.opExtrude","CAP_EDGE",EDGE,{"disambiguationData":[OSD([subQ1]),TDD([subQ3])],"isStart":false}),makeQuery(id+"F6.boolean.opBoolean","COPY",FACE,{"disambiguationData":[TD([makeQuery(id+"F2.opExtrude","SWEPT_FACE",FACE,{"disambiguationData":[OSD([subQ0])]})])],"derivedFrom":makeQuery(id+"F6.opExtrude","SWEPT_FACE",FACE,{"disambiguationData":[OSD([subQ4])]})})],"blendedInto":[makeQuery(id+"F6.boolean.opBoolean","COPY",FACE,{"disambiguationData":[TD([makeQuery(id+"F2.opExtrude","SWEPT_FACE",FACE,{"disambiguationData":[OSD([subQ0])]})])],"derivedFrom":makeQuery(id+"F6.opExtrude","SWEPT_FACE",FACE,{"disambiguationData":[OSD([subQ4])]})})]})])],"isStart":false})])],"isStart":false})])]});}
            extrude(context, id + "F18", {"entities" : qUnion([Q0, Q1]), "operationType" : NewBodyOperationType.ADD, "oppositeDirection" : true, "depth" : 1 * mm});
        }
        {
            var Q0;
            {var subQ0=sQuery(id+"F0.wireOp",EDGE,"E19");var subQ1=sQuery(id+"F0.wireOp",EDGE,"E18.bottom");var subQ3=makeQuery(id+"F0.imprint","IMPRINT",EDGE,{"disambiguationData":[TD([[makeQuery(id+"F0.imprint","INTERSECT",VERTEX,{"derivedFrom":[subQ1,subQ0]}),1.0]])],"derivedFrom":subQ0});var subQ4=makeQuery(id+"F3.opExtrude","CAP_EDGE",EDGE,{"disambiguationData":[OSD([subQ0]),TDD([subQ3])],"isStart":false});var subQ5=sQuery(id+"F5.wireOp",EDGE,"E54.top");Q0=makeQuery(id+"F13.opChamfer","BLEND_EDGE",EDGE,{"blendedFrom":[makeQuery(id+"F12.opExtrude","CAP_EDGE",EDGE,{"disambiguationData":[OSD([subQ0,subQ5]),TDD([makeQuery(id+"F11.opExtrude","CAP_EDGE",EDGE,{"disambiguationData":[OSD([subQ0,subQ5]),TDD([makeQuery(id+"F10.opChamfer","BLEND_EDGE",EDGE,{"blendedFrom":[subQ4,makeQuery(id+"F6.boolean.opBoolean","COPY",FACE,{"disambiguationData":[TD([makeQuery(id+"F2.opExtrude","SWEPT_FACE",FACE,{"disambiguationData":[OSD([subQ1])]})])],"derivedFrom":makeQuery(id+"F6.opExtrude","SWEPT_FACE",FACE,{"disambiguationData":[OSD([subQ5])]})})],"blendedInto":[makeQuery(id+"F6.boolean.opBoolean","COPY",FACE,{"disambiguationData":[TD([makeQuery(id+"F2.opExtrude","SWEPT_FACE",FACE,{"disambiguationData":[OSD([subQ1])]})])],"derivedFrom":makeQuery(id+"F6.opExtrude","SWEPT_FACE",FACE,{"disambiguationData":[OSD([subQ5])]})})]})])],"isStart":false})])],"isStart":false}),makeQuery(id+"F12.opExtrude","CAP_FACE",FACE,{"disambiguationData":[OSD([subQ0]),TDD([makeQuery(id+"F11.opExtrude","CAP_FACE",FACE,{"disambiguationData":[OSD([subQ0]),TDD([makeQuery(id+"F10.opChamfer","BLEND_FACE",FACE,{"disambiguationData":[OSD([subQ0]),TDD([subQ4])]})])],"isStart":false})])],"isStart":false})],"blendedInto":[makeQuery(id+"F12.opExtrude","CAP_FACE",FACE,{"disambiguationData":[OSD([subQ0]),TDD([makeQuery(id+"F11.opExtrude","CAP_FACE",FACE,{"disambiguationData":[OSD([subQ0]),TDD([makeQuery(id+"F10.opChamfer","BLEND_FACE",FACE,{"disambiguationData":[OSD([subQ0]),TDD([subQ4])]})])],"isStart":false})])],"isStart":false})]});}
            var Q1;
            {var subQ0=sQuery(id+"F0.wireOp",EDGE,"E25");var subQ1=sQuery(id+"F0.wireOp",EDGE,"E19");var subQ3=makeQuery(id+"F0.imprint","IMPRINT",EDGE,{"disambiguationData":[TD([[makeQuery(id+"F0.imprint","INTERSECT",VERTEX,{"derivedFrom":[subQ1,subQ0]}),-1.0]])],"derivedFrom":subQ1});var subQ4=makeQuery(id+"F3.opExtrude","CAP_EDGE",EDGE,{"disambiguationData":[OSD([subQ1]),TDD([subQ3])],"isStart":false});var subQ5=sQuery(id+"F5.wireOp",EDGE,"E54.top");Q1=makeQuery(id+"F13.opChamfer","BLEND_EDGE",EDGE,{"blendedFrom":[makeQuery(id+"F12.opExtrude","CAP_EDGE",EDGE,{"disambiguationData":[OSD([subQ1,subQ5]),TDD([makeQuery(id+"F11.opExtrude","CAP_EDGE",EDGE,{"disambiguationData":[OSD([subQ1,subQ5]),TDD([makeQuery(id+"F10.opChamfer","BLEND_EDGE",EDGE,{"blendedFrom":[subQ4,makeQuery(id+"F6.boolean.opBoolean","COPY",FACE,{"disambiguationData":[TD([makeQuery(id+"F2.opExtrude","SWEPT_FACE",FACE,{"disambiguationData":[OSD([subQ0])]})])],"derivedFrom":makeQuery(id+"F6.opExtrude","SWEPT_FACE",FACE,{"disambiguationData":[OSD([subQ5])]})})],"blendedInto":[makeQuery(id+"F6.boolean.opBoolean","COPY",FACE,{"disambiguationData":[TD([makeQuery(id+"F2.opExtrude","SWEPT_FACE",FACE,{"disambiguationData":[OSD([subQ0])]})])],"derivedFrom":makeQuery(id+"F6.opExtrude","SWEPT_FACE",FACE,{"disambiguationData":[OSD([subQ5])]})})]})])],"isStart":false})])],"isStart":false}),makeQuery(id+"F12.opExtrude","CAP_FACE",FACE,{"disambiguationData":[OSD([subQ1]),TDD([makeQuery(id+"F11.opExtrude","CAP_FACE",FACE,{"disambiguationData":[OSD([subQ1]),TDD([makeQuery(id+"F10.opChamfer","BLEND_FACE",FACE,{"disambiguationData":[OSD([subQ1]),TDD([subQ4])]})])],"isStart":false})])],"isStart":false})],"blendedInto":[makeQuery(id+"F12.opExtrude","CAP_FACE",FACE,{"disambiguationData":[OSD([subQ1]),TDD([makeQuery(id+"F11.opExtrude","CAP_FACE",FACE,{"disambiguationData":[OSD([subQ1]),TDD([makeQuery(id+"F10.opChamfer","BLEND_FACE",FACE,{"disambiguationData":[OSD([subQ1]),TDD([subQ4])]})])],"isStart":false})])],"isStart":false})]});}
            var Q2;
            Q2=makeQuery(id+"F4.opExtrude","CAP_EDGE",EDGE,{"disambiguationData":[OSD([sQuery(id+"F0.wireOp",EDGE,"E18.right")])],"isStart":false});
            var Q3;
            {var subQ0=sQuery(id+"F0.wireOp",EDGE,"E18.right");Q3=makeQuery(id+"F9.opChamfer","BLEND_EDGE",EDGE,{"blendedFrom":[makeQuery(id+"F4.opExtrude","CAP_EDGE",EDGE,{"disambiguationData":[OSD([subQ0])],"isStart":true}),makeQuery(id+"F4.opExtrude","SWEPT_FACE",FACE,{"disambiguationData":[OSD([subQ0])]})],"blendedInto":[makeQuery(id+"F4.opExtrude","SWEPT_FACE",FACE,{"disambiguationData":[OSD([subQ0])]})]});}
            fillet(context, id + "F19", {"entities" : qUnion([Q0, Q1, Q2, Q3]), "radius" : 1 * mm, "allowEdgeOverflow" : false});
        }
        {
            var Q0;
            {var subQ0=sQuery(id+"F0.wireOp",EDGE,"E28");var subQ1=sQuery(id+"F0.wireOp",EDGE,"E21");var subQ2=sQuery(id+"F0.wireOp",EDGE,"E19");var subQ3=sQuery(id+"F0.wireOp",EDGE,"E18.bottom");var subQ4=makeQuery(id+"F10.opChamfer","BLEND_VERTEX",VERTEX,{"blendedFrom":[makeQuery(id+"F3.opExtrude","CAP_EDGE",EDGE,{"disambiguationData":[OSD([subQ2]),TDD([makeQuery(id+"F0.imprint","IMPRINT",EDGE,{"disambiguationData":[TD([[makeQuery(id+"F0.imprint","INTERSECT",VERTEX,{"derivedFrom":[subQ3,subQ2]}),1.0]])],"derivedFrom":subQ2})])],"isStart":false}),makeQuery(id+"F3.opExtrude","CAP_FACE",FACE,{"disambiguationData":[OSD([subQ3,subQ2,subQ1,subQ0])],"isStart":false}),makeQuery(id+"F3.boolean.opBoolean","MERGE",FACE,{"derivedFrom":[makeQuery(id+"F2.opExtrude","SWEPT_FACE",FACE,{"disambiguationData":[OSD([subQ0])]}),makeQuery(id+"F3.opExtrude","SWEPT_FACE",FACE,{"disambiguationData":[OSD([subQ0])]})]})],"blendedInto":[makeQuery(id+"F3.opExtrude","CAP_FACE",FACE,{"disambiguationData":[OSD([subQ3,subQ2,subQ1,subQ0])],"isStart":false}),makeQuery(id+"F3.boolean.opBoolean","MERGE",FACE,{"derivedFrom":[makeQuery(id+"F2.opExtrude","SWEPT_FACE",FACE,{"disambiguationData":[OSD([subQ0])]}),makeQuery(id+"F3.opExtrude","SWEPT_FACE",FACE,{"disambiguationData":[OSD([subQ0])]})]})]});Q0=makeQuery(id+"F15.opExtrude","CAP_EDGE",EDGE,{"disambiguationData":[OSD([subQ3,subQ2,subQ1,subQ0]),TDD([makeQuery(id+"F12.boolean.opBoolean","MERGE",EDGE,{"derivedFrom":[makeQuery(id+"F11.opExtrude","SWEPT_EDGE",EDGE,{"disambiguationData":[OSD([subQ3,subQ2,subQ1,subQ0]),TDD([subQ4])]}),makeQuery(id+"F12.opExtrude","SWEPT_EDGE",EDGE,{"disambiguationData":[OSD([subQ3,subQ2,subQ1,subQ0]),TDD([makeQuery(id+"F11.opExtrude","CAP_VERTEX",VERTEX,{"disambiguationData":[OSD([subQ3,subQ2,subQ1,subQ0]),TDD([subQ4])],"isStart":false})])]})]})])],"isStart":false});}
            var Q1;
            {var subQ0=sQuery(id+"F0.wireOp",EDGE,"E26");var subQ1=sQuery(id+"F0.wireOp",EDGE,"E25");var subQ2=sQuery(id+"F0.wireOp",EDGE,"E21");var subQ3=sQuery(id+"F0.wireOp",EDGE,"E19");var subQ4=makeQuery(id+"F10.opChamfer","BLEND_VERTEX",VERTEX,{"blendedFrom":[makeQuery(id+"F3.opExtrude","CAP_EDGE",EDGE,{"disambiguationData":[OSD([subQ3]),TDD([makeQuery(id+"F0.imprint","IMPRINT",EDGE,{"disambiguationData":[TD([[makeQuery(id+"F0.imprint","INTERSECT",VERTEX,{"derivedFrom":[subQ3,subQ1]}),-1.0]])],"derivedFrom":subQ3})])],"isStart":false}),makeQuery(id+"F3.opExtrude","CAP_FACE",FACE,{"disambiguationData":[OSD([subQ3,subQ2,subQ1,subQ0])],"isStart":false}),makeQuery(id+"F3.boolean.opBoolean","MERGE",FACE,{"derivedFrom":[makeQuery(id+"F2.opExtrude","SWEPT_FACE",FACE,{"disambiguationData":[OSD([subQ0])]}),makeQuery(id+"F3.opExtrude","SWEPT_FACE",FACE,{"disambiguationData":[OSD([subQ0])]})]})],"blendedInto":[makeQuery(id+"F3.opExtrude","CAP_FACE",FACE,{"disambiguationData":[OSD([subQ3,subQ2,subQ1,subQ0])],"isStart":false}),makeQuery(id+"F3.boolean.opBoolean","MERGE",FACE,{"derivedFrom":[makeQuery(id+"F2.opExtrude","SWEPT_FACE",FACE,{"disambiguationData":[OSD([subQ0])]}),makeQuery(id+"F3.opExtrude","SWEPT_FACE",FACE,{"disambiguationData":[OSD([subQ0])]})]})]});Q1=makeQuery(id+"F15.opExtrude","CAP_EDGE",EDGE,{"disambiguationData":[OSD([subQ3,subQ2,subQ1,subQ0]),TDD([makeQuery(id+"F12.boolean.opBoolean","MERGE",EDGE,{"derivedFrom":[makeQuery(id+"F11.opExtrude","SWEPT_EDGE",EDGE,{"disambiguationData":[OSD([subQ3,subQ2,subQ1,subQ0]),TDD([subQ4])]}),makeQuery(id+"F12.opExtrude","SWEPT_EDGE",EDGE,{"disambiguationData":[OSD([subQ3,subQ2,subQ1,subQ0]),TDD([makeQuery(id+"F11.opExtrude","CAP_VERTEX",VERTEX,{"disambiguationData":[OSD([subQ3,subQ2,subQ1,subQ0]),TDD([subQ4])],"isStart":false})])]})]})])],"isStart":false});}
            var Q2;
            {var subQ0=sQuery(id+"F0.wireOp",EDGE,"E25");var subQ1=sQuery(id+"F0.wireOp",EDGE,"E26");var subQ2=sQuery(id+"F0.wireOp",EDGE,"E21");var subQ3=sQuery(id+"F0.wireOp",EDGE,"E19");var subQ4=makeQuery(id+"F10.opChamfer","BLEND_VERTEX",VERTEX,{"blendedFrom":[makeQuery(id+"F3.opExtrude","CAP_EDGE",EDGE,{"disambiguationData":[OSD([subQ3]),TDD([makeQuery(id+"F0.imprint","IMPRINT",EDGE,{"disambiguationData":[TD([[makeQuery(id+"F0.imprint","INTERSECT",VERTEX,{"derivedFrom":[subQ3,subQ0]}),-1.0]])],"derivedFrom":subQ3})])],"isStart":false}),makeQuery(id+"F3.opExtrude","CAP_FACE",FACE,{"disambiguationData":[OSD([subQ3,subQ2,subQ0,subQ1])],"isStart":false}),makeQuery(id+"F3.boolean.opBoolean","MERGE",FACE,{"derivedFrom":[makeQuery(id+"F2.opExtrude","SWEPT_FACE",FACE,{"disambiguationData":[OSD([subQ0])]}),makeQuery(id+"F3.opExtrude","SWEPT_FACE",FACE,{"disambiguationData":[OSD([subQ0])]})]})],"blendedInto":[makeQuery(id+"F3.opExtrude","CAP_FACE",FACE,{"disambiguationData":[OSD([subQ3,subQ2,subQ0,subQ1])],"isStart":false}),makeQuery(id+"F3.boolean.opBoolean","MERGE",FACE,{"derivedFrom":[makeQuery(id+"F2.opExtrude","SWEPT_FACE",FACE,{"disambiguationData":[OSD([subQ0])]}),makeQuery(id+"F3.opExtrude","SWEPT_FACE",FACE,{"disambiguationData":[OSD([subQ0])]})]})]});Q2=makeQuery(id+"F15.opExtrude","CAP_EDGE",EDGE,{"disambiguationData":[OSD([subQ3,subQ2,subQ0,subQ1]),TDD([makeQuery(id+"F12.boolean.opBoolean","MERGE",EDGE,{"derivedFrom":[makeQuery(id+"F11.opExtrude","SWEPT_EDGE",EDGE,{"disambiguationData":[OSD([subQ3,subQ2,subQ0,subQ1]),TDD([subQ4])]}),makeQuery(id+"F12.opExtrude","SWEPT_EDGE",EDGE,{"disambiguationData":[OSD([subQ3,subQ2,subQ0,subQ1]),TDD([makeQuery(id+"F11.opExtrude","CAP_VERTEX",VERTEX,{"disambiguationData":[OSD([subQ3,subQ2,subQ0,subQ1]),TDD([subQ4])],"isStart":false})])]})]})])],"isStart":false});}
            var Q3;
            {var subQ0=sQuery(id+"F0.wireOp",EDGE,"E23");var subQ1=sQuery(id+"F0.wireOp",EDGE,"E29");var subQ2=sQuery(id+"F0.wireOp",EDGE,"E21");var subQ3=sQuery(id+"F0.wireOp",EDGE,"E19");var subQ4=makeQuery(id+"F10.opChamfer","BLEND_VERTEX",VERTEX,{"blendedFrom":[makeQuery(id+"F3.opExtrude","CAP_EDGE",EDGE,{"disambiguationData":[OSD([subQ3]),TDD([makeQuery(id+"F0.imprint","IMPRINT",EDGE,{"disambiguationData":[TD([[makeQuery(id+"F0.imprint","INTERSECT",VERTEX,{"derivedFrom":[subQ3,subQ1]}),-1.0]])],"derivedFrom":subQ3})])],"isStart":false}),makeQuery(id+"F3.opExtrude","CAP_FACE",FACE,{"disambiguationData":[OSD([subQ3,subQ2,subQ0,subQ1])],"isStart":false}),makeQuery(id+"F3.boolean.opBoolean","MERGE",FACE,{"derivedFrom":[makeQuery(id+"F2.opExtrude","SWEPT_FACE",FACE,{"disambiguationData":[OSD([subQ0])]}),makeQuery(id+"F3.opExtrude","SWEPT_FACE",FACE,{"disambiguationData":[OSD([subQ0])]})]})],"blendedInto":[makeQuery(id+"F3.opExtrude","CAP_FACE",FACE,{"disambiguationData":[OSD([subQ3,subQ2,subQ0,subQ1])],"isStart":false}),makeQuery(id+"F3.boolean.opBoolean","MERGE",FACE,{"derivedFrom":[makeQuery(id+"F2.opExtrude","SWEPT_FACE",FACE,{"disambiguationData":[OSD([subQ0])]}),makeQuery(id+"F3.opExtrude","SWEPT_FACE",FACE,{"disambiguationData":[OSD([subQ0])]})]})]});Q3=makeQuery(id+"F15.opExtrude","CAP_EDGE",EDGE,{"disambiguationData":[OSD([subQ3,subQ2,subQ0,subQ1]),TDD([makeQuery(id+"F12.boolean.opBoolean","MERGE",EDGE,{"derivedFrom":[makeQuery(id+"F11.opExtrude","SWEPT_EDGE",EDGE,{"disambiguationData":[OSD([subQ3,subQ2,subQ0,subQ1]),TDD([subQ4])]}),makeQuery(id+"F12.opExtrude","SWEPT_EDGE",EDGE,{"disambiguationData":[OSD([subQ3,subQ2,subQ0,subQ1]),TDD([makeQuery(id+"F11.opExtrude","CAP_VERTEX",VERTEX,{"disambiguationData":[OSD([subQ3,subQ2,subQ0,subQ1]),TDD([subQ4])],"isStart":false})])]})]})])],"isStart":false});}
            var Q4;
            {var subQ0=sQuery(id+"F0.wireOp",EDGE,"E29");var subQ1=sQuery(id+"F0.wireOp",EDGE,"E23");var subQ2=sQuery(id+"F0.wireOp",EDGE,"E21");var subQ3=sQuery(id+"F0.wireOp",EDGE,"E19");var subQ4=makeQuery(id+"F10.opChamfer","BLEND_VERTEX",VERTEX,{"blendedFrom":[makeQuery(id+"F3.opExtrude","CAP_EDGE",EDGE,{"disambiguationData":[OSD([subQ3]),TDD([makeQuery(id+"F0.imprint","IMPRINT",EDGE,{"disambiguationData":[TD([[makeQuery(id+"F0.imprint","INTERSECT",VERTEX,{"derivedFrom":[subQ3,subQ0]}),-1.0]])],"derivedFrom":subQ3})])],"isStart":false}),makeQuery(id+"F3.opExtrude","CAP_FACE",FACE,{"disambiguationData":[OSD([subQ3,subQ2,subQ1,subQ0])],"isStart":false}),makeQuery(id+"F3.boolean.opBoolean","MERGE",FACE,{"derivedFrom":[makeQuery(id+"F2.opExtrude","SWEPT_FACE",FACE,{"disambiguationData":[OSD([subQ0])]}),makeQuery(id+"F3.opExtrude","SWEPT_FACE",FACE,{"disambiguationData":[OSD([subQ0])]})]})],"blendedInto":[makeQuery(id+"F3.opExtrude","CAP_FACE",FACE,{"disambiguationData":[OSD([subQ3,subQ2,subQ1,subQ0])],"isStart":false}),makeQuery(id+"F3.boolean.opBoolean","MERGE",FACE,{"derivedFrom":[makeQuery(id+"F2.opExtrude","SWEPT_FACE",FACE,{"disambiguationData":[OSD([subQ0])]}),makeQuery(id+"F3.opExtrude","SWEPT_FACE",FACE,{"disambiguationData":[OSD([subQ0])]})]})]});Q4=makeQuery(id+"F15.opExtrude","CAP_EDGE",EDGE,{"disambiguationData":[OSD([subQ3,subQ2,subQ1,subQ0]),TDD([makeQuery(id+"F12.boolean.opBoolean","MERGE",EDGE,{"derivedFrom":[makeQuery(id+"F11.opExtrude","SWEPT_EDGE",EDGE,{"disambiguationData":[OSD([subQ3,subQ2,subQ1,subQ0]),TDD([subQ4])]}),makeQuery(id+"F12.opExtrude","SWEPT_EDGE",EDGE,{"disambiguationData":[OSD([subQ3,subQ2,subQ1,subQ0]),TDD([makeQuery(id+"F11.opExtrude","CAP_VERTEX",VERTEX,{"disambiguationData":[OSD([subQ3,subQ2,subQ1,subQ0]),TDD([subQ4])],"isStart":false})])]})]})])],"isStart":false});}
            var Q5;
            {var subQ0=sQuery(id+"F0.wireOp",EDGE,"E31");var subQ1=sQuery(id+"F0.wireOp",EDGE,"E21");var subQ2=sQuery(id+"F0.wireOp",EDGE,"E19");var subQ3=sQuery(id+"F0.wireOp",EDGE,"E18.top");var subQ4=makeQuery(id+"F10.opChamfer","BLEND_VERTEX",VERTEX,{"blendedFrom":[makeQuery(id+"F3.opExtrude","CAP_EDGE",EDGE,{"disambiguationData":[OSD([subQ2]),TDD([makeQuery(id+"F0.imprint","IMPRINT",EDGE,{"disambiguationData":[TD([[makeQuery(id+"F0.imprint","INTERSECT",VERTEX,{"derivedFrom":[subQ3,subQ2]}),-1.0]])],"derivedFrom":subQ2})])],"isStart":false}),makeQuery(id+"F3.opExtrude","CAP_FACE",FACE,{"disambiguationData":[OSD([subQ3,subQ2,subQ1,subQ0])],"isStart":false}),makeQuery(id+"F3.boolean.opBoolean","MERGE",FACE,{"derivedFrom":[makeQuery(id+"F2.opExtrude","SWEPT_FACE",FACE,{"disambiguationData":[OSD([subQ0])]}),makeQuery(id+"F3.opExtrude","SWEPT_FACE",FACE,{"disambiguationData":[OSD([subQ0])]})]})],"blendedInto":[makeQuery(id+"F3.opExtrude","CAP_FACE",FACE,{"disambiguationData":[OSD([subQ3,subQ2,subQ1,subQ0])],"isStart":false}),makeQuery(id+"F3.boolean.opBoolean","MERGE",FACE,{"derivedFrom":[makeQuery(id+"F2.opExtrude","SWEPT_FACE",FACE,{"disambiguationData":[OSD([subQ0])]}),makeQuery(id+"F3.opExtrude","SWEPT_FACE",FACE,{"disambiguationData":[OSD([subQ0])]})]})]});Q5=makeQuery(id+"F15.opExtrude","CAP_EDGE",EDGE,{"disambiguationData":[OSD([subQ3,subQ2,subQ1,subQ0]),TDD([makeQuery(id+"F12.boolean.opBoolean","MERGE",EDGE,{"derivedFrom":[makeQuery(id+"F11.opExtrude","SWEPT_EDGE",EDGE,{"disambiguationData":[OSD([subQ3,subQ2,subQ1,subQ0]),TDD([subQ4])]}),makeQuery(id+"F12.opExtrude","SWEPT_EDGE",EDGE,{"disambiguationData":[OSD([subQ3,subQ2,subQ1,subQ0]),TDD([makeQuery(id+"F11.opExtrude","CAP_VERTEX",VERTEX,{"disambiguationData":[OSD([subQ3,subQ2,subQ1,subQ0]),TDD([subQ4])],"isStart":false})])]})]})])],"isStart":false});}
            chamfer(context, id + "F20", {"entities" : qUnion([Q0, Q1, Q2, Q3, Q4, Q5]), "width" : 1 * mm});
        }
        {
            var Q0;
            Q0=makeQuery(id+"F1.opExtrude","SWEPT_EDGE",EDGE,{"disambiguationData":[OSD([sQuery(id+"F0.wireOp",EDGE,"E18.top"),sQuery(id+"F0.wireOp",EDGE,"E51.bottom"),sQuery(id+"F0.wireOp",EDGE,"E51.left")])]});
            var Q1;
            Q1=makeQuery(id+"F1.opExtrude","SWEPT_EDGE",EDGE,{"disambiguationData":[OSD([sQuery(id+"F0.wireOp",EDGE,"E51.left"),sQuery(id+"F0.wireOp",EDGE,"E53.bottom")])]});
            var Q2;
            Q2=makeQuery(id+"F1.opExtrude","SWEPT_EDGE",EDGE,{"disambiguationData":[OSD([sQuery(id+"F0.wireOp",EDGE,"E53.bottom"),sQuery(id+"F0.wireOp",EDGE,"E53.right")])]});
            var Q3;
            Q3=makeQuery(id+"F1.opExtrude","SWEPT_EDGE",EDGE,{"disambiguationData":[OSD([sQuery(id+"F0.wireOp",EDGE,"E53.top"),sQuery(id+"F0.wireOp",EDGE,"E53.right")])]});
            var Q4;
            Q4=makeQuery(id+"F1.opExtrude","SWEPT_EDGE",EDGE,{"disambiguationData":[OSD([sQuery(id+"F0.wireOp",EDGE,"E51.right"),sQuery(id+"F0.wireOp",EDGE,"E53.bottom")])]});
            var Q5;
            Q5=makeQuery(id+"F1.opExtrude","SWEPT_EDGE",EDGE,{"disambiguationData":[OSD([sQuery(id+"F0.wireOp",EDGE,"E53.bottom"),sQuery(id+"F0.wireOp",EDGE,"E53.left")])]});
            var Q6;
            Q6=makeQuery(id+"F1.opExtrude","SWEPT_EDGE",EDGE,{"disambiguationData":[OSD([sQuery(id+"F0.wireOp",EDGE,"E53.top"),sQuery(id+"F0.wireOp",EDGE,"E53.left")])]});
            var Q7;
            Q7=makeQuery(id+"F1.opExtrude","SWEPT_EDGE",EDGE,{"disambiguationData":[OSD([sQuery(id+"F0.wireOp",EDGE,"E18.top"),sQuery(id+"F0.wireOp",EDGE,"E51.bottom"),sQuery(id+"F0.wireOp",EDGE,"E51.right")])]});
            var Q8;
            Q8=makeQuery(id+"F1.opExtrude","SWEPT_EDGE",EDGE,{"disambiguationData":[OSD([sQuery(id+"F0.wireOp",EDGE,"E18.top"),sQuery(id+"F0.wireOp",EDGE,"E48.bottom"),sQuery(id+"F0.wireOp",EDGE,"E48.right")])]});
            var Q9;
            Q9=makeQuery(id+"F1.opExtrude","SWEPT_EDGE",EDGE,{"disambiguationData":[OSD([sQuery(id+"F0.wireOp",EDGE,"E48.right"),sQuery(id+"F0.wireOp",EDGE,"E50.bottom")])]});
            var Q10;
            Q10=makeQuery(id+"F1.opExtrude","SWEPT_EDGE",EDGE,{"disambiguationData":[OSD([sQuery(id+"F0.wireOp",EDGE,"E50.top"),sQuery(id+"F0.wireOp",EDGE,"E50.left")])]});
            var Q11;
            Q11=makeQuery(id+"F1.opExtrude","SWEPT_EDGE",EDGE,{"disambiguationData":[OSD([sQuery(id+"F0.wireOp",EDGE,"E18.top"),sQuery(id+"F0.wireOp",EDGE,"E48.bottom"),sQuery(id+"F0.wireOp",EDGE,"E48.left")])]});
            var Q12;
            Q12=makeQuery(id+"F1.opExtrude","SWEPT_EDGE",EDGE,{"disambiguationData":[OSD([sQuery(id+"F0.wireOp",EDGE,"E48.left"),sQuery(id+"F0.wireOp",EDGE,"E50.bottom")])]});
            var Q13;
            Q13=makeQuery(id+"F1.opExtrude","SWEPT_EDGE",EDGE,{"disambiguationData":[OSD([sQuery(id+"F0.wireOp",EDGE,"E50.bottom"),sQuery(id+"F0.wireOp",EDGE,"E50.right")])]});
            var Q14;
            Q14=makeQuery(id+"F1.opExtrude","SWEPT_EDGE",EDGE,{"disambiguationData":[OSD([sQuery(id+"F0.wireOp",EDGE,"E50.top"),sQuery(id+"F0.wireOp",EDGE,"E50.right")])]});
            var Q15;
            Q15=makeQuery(id+"F1.opExtrude","SWEPT_EDGE",EDGE,{"disambiguationData":[OSD([sQuery(id+"F0.wireOp",EDGE,"E45.top"),sQuery(id+"F0.wireOp",EDGE,"E45.left")])]});
            var Q16;
            Q16=makeQuery(id+"F1.opExtrude","SWEPT_EDGE",EDGE,{"disambiguationData":[OSD([sQuery(id+"F0.wireOp",EDGE,"E45.top"),sQuery(id+"F0.wireOp",EDGE,"E45.right")])]});
            var Q17;
            Q17=makeQuery(id+"F1.opExtrude","SWEPT_EDGE",EDGE,{"disambiguationData":[OSD([sQuery(id+"F0.wireOp",EDGE,"E44.left"),sQuery(id+"F0.wireOp",EDGE,"E45.bottom")])]});
            var Q18;
            Q18=makeQuery(id+"F1.opExtrude","SWEPT_EDGE",EDGE,{"disambiguationData":[OSD([sQuery(id+"F0.wireOp",EDGE,"E45.bottom"),sQuery(id+"F0.wireOp",EDGE,"E45.left")])]});
            var Q19;
            Q19=makeQuery(id+"F1.opExtrude","SWEPT_EDGE",EDGE,{"disambiguationData":[OSD([sQuery(id+"F0.wireOp",EDGE,"E45.bottom"),sQuery(id+"F0.wireOp",EDGE,"E45.right")])]});
            var Q20;
            Q20=makeQuery(id+"F1.opExtrude","SWEPT_EDGE",EDGE,{"disambiguationData":[OSD([sQuery(id+"F0.wireOp",EDGE,"E44.right"),sQuery(id+"F0.wireOp",EDGE,"E45.bottom")])]});
            var Q21;
            Q21=makeQuery(id+"F1.opExtrude","SWEPT_EDGE",EDGE,{"disambiguationData":[OSD([sQuery(id+"F0.wireOp",EDGE,"E18.bottom"),sQuery(id+"F0.wireOp",EDGE,"E44.bottom"),sQuery(id+"F0.wireOp",EDGE,"E44.left")])]});
            var Q22;
            Q22=makeQuery(id+"F1.opExtrude","SWEPT_EDGE",EDGE,{"disambiguationData":[OSD([sQuery(id+"F0.wireOp",EDGE,"E18.bottom"),sQuery(id+"F0.wireOp",EDGE,"E44.bottom"),sQuery(id+"F0.wireOp",EDGE,"E44.right")])]});
            var Q23;
            Q23=makeQuery(id+"F1.opExtrude","SWEPT_EDGE",EDGE,{"disambiguationData":[OSD([sQuery(id+"F0.wireOp",EDGE,"E18.bottom"),sQuery(id+"F0.wireOp",EDGE,"E41.bottom"),sQuery(id+"F0.wireOp",EDGE,"E41.left")])]});
            var Q24;
            Q24=makeQuery(id+"F1.opExtrude","SWEPT_EDGE",EDGE,{"disambiguationData":[OSD([sQuery(id+"F0.wireOp",EDGE,"E41.left"),sQuery(id+"F0.wireOp",EDGE,"E42.bottom")])]});
            var Q25;
            Q25=makeQuery(id+"F1.opExtrude","SWEPT_EDGE",EDGE,{"disambiguationData":[OSD([sQuery(id+"F0.wireOp",EDGE,"E42.top"),sQuery(id+"F0.wireOp",EDGE,"E42.left")])]});
            var Q26;
            Q26=makeQuery(id+"F1.opExtrude","SWEPT_EDGE",EDGE,{"disambiguationData":[OSD([sQuery(id+"F0.wireOp",EDGE,"E42.top"),sQuery(id+"F0.wireOp",EDGE,"E42.right")])]});
            var Q27;
            Q27=makeQuery(id+"F1.opExtrude","SWEPT_EDGE",EDGE,{"disambiguationData":[OSD([sQuery(id+"F0.wireOp",EDGE,"E41.right"),sQuery(id+"F0.wireOp",EDGE,"E42.bottom")])]});
            var Q28;
            Q28=makeQuery(id+"F1.opExtrude","SWEPT_EDGE",EDGE,{"disambiguationData":[OSD([sQuery(id+"F0.wireOp",EDGE,"E18.bottom"),sQuery(id+"F0.wireOp",EDGE,"E41.bottom"),sQuery(id+"F0.wireOp",EDGE,"E41.right")])]});
            var Q29;
            Q29=makeQuery(id+"F1.opExtrude","SWEPT_EDGE",EDGE,{"disambiguationData":[OSD([sQuery(id+"F0.wireOp",EDGE,"E42.bottom"),sQuery(id+"F0.wireOp",EDGE,"E42.right")])]});
            var Q30;
            Q30=makeQuery(id+"F1.opExtrude","SWEPT_EDGE",EDGE,{"disambiguationData":[OSD([sQuery(id+"F0.wireOp",EDGE,"E42.bottom"),sQuery(id+"F0.wireOp",EDGE,"E42.left")])]});
            fillet(context, id + "F21", {"entities" : qUnion([Q0, Q1, Q2, Q3, Q4, Q5, Q6, Q7, Q8, Q9, Q10, Q11, Q12, Q13, Q14, Q15, Q16, Q17, Q18, Q19, Q20, Q21, Q22, Q23, Q24, Q25, Q26, Q27, Q28, Q29, Q30]), "radius" : 1 * mm, "allowEdgeOverflow" : false});
        }
    });
